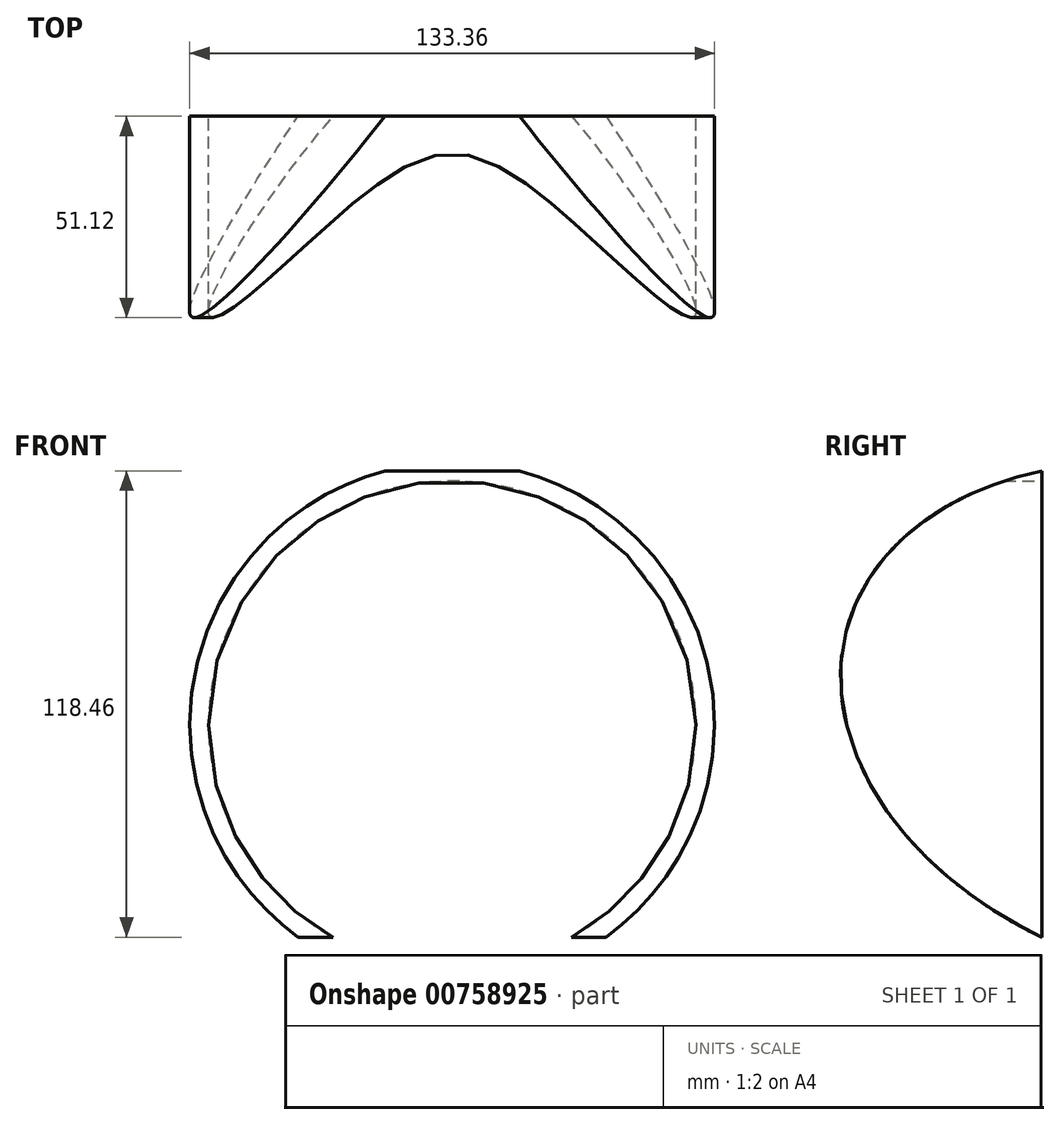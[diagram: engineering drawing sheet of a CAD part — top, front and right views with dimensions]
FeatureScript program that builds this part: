
annotation { "Feature Type Name" : "Feature", "Feature Type Description" : "" }
export const myFeature = defineFeature(function(context is Context, id is Id, definition is map)
    precondition{}
    {
        {
            var Q0;
            Q0=qCreatedBy(makeId("Front.planeOp"),FACE);
            var sketch = newSketch(context, id + "F0", { "sketchPlane" : qUnion([Q0])});
            skArc(sketch, "E0", {"start": v(63.5, 0) * mm, "mid": v(0, 63.5) * mm, "end": v(-63.5, 0) * mm});
            skArc(sketch, "E1", {"start": v(61.9, 1.59) * mm, "mid": v(43.78, 43.78) * mm, "end": v(1.59, 61.9) * mm});
            skArc(sketch, "E2", {"start": v(15.19, 36.67) * mm, "mid": v(8.52, 38.76) * mm, "end": v(1.59, 39.66) * mm});
            skLineSegment(sketch, "E3.0", {"start": v(1.59, 39.66) * mm, "end": v(1.59, 61.9) * mm});
            skLineSegment(sketch, "E4.0", {"start": v(-1.59, 39.66) * mm, "end": v(-1.59, 61.9) * mm});
            skLineSegment(sketch, "E5.1.0", {"start": v(0, -0.01) * mm, "end": v(0, 0) * mm});
            skLineSegment(sketch, "E5.6.1", {"start": v(-1.59, -3.83) * mm, "end": v(-25.8, -28.04) * mm});
            skLineSegment(sketch, "E5.7.1", {"start": v(-13.7, -37.24) * mm, "end": v(-22.22, -57.79) * mm});
            skLineSegment(sketch, "E5.7.2", {"start": v(-16.64, -36.03) * mm, "end": v(-25.15, -56.57) * mm});
            skLineSegment(sketch, "E5.8.1", {"start": v(1.59, -3.83) * mm, "end": v(1.59, -38.07) * mm});
            skLineSegment(sketch, "E5.8.2", {"start": v(-1.59, -3.83) * mm, "end": v(-1.59, -38.07) * mm});
            skLineSegment(sketch, "E5.9.1", {"start": v(16.64, -36.03) * mm, "end": v(25.15, -56.57) * mm});
            skLineSegment(sketch, "E5.9.2", {"start": v(13.7, -37.24) * mm, "end": v(22.22, -57.79) * mm});
            skLineSegment(sketch, "E6", {"start": v(63.5, 0) * mm, "end": v(63.5, 63.64) * mm});
            skLineSegment(sketch, "E7", {"start": v(23.7, 63.5) * mm, "end": v(63.5, 63.5) * mm});
            skLineSegment(sketch, "E8", {"start": v(-63.5, 0) * mm, "end": v(-61.9, 63.5) * mm});
            skLineSegment(sketch, "E9", {"start": v(-61.9, 63.5) * mm, "end": v(-23.7, 63.5) * mm});
            skLineSegment(sketch, "E10", {"start": v(-23.7, 58.91) * mm, "end": v(-23.7, 63.5) * mm});
            skLineSegment(sketch, "E11", {"start": v(23.7, 58.91) * mm, "end": v(23.7, 63.5) * mm});
            skPoint(sketch, "E5.12.0.end.orphan", {"position": v(61.91, 0) * mm});
            skPoint(sketch, "E12.orphan", {"position": v(0, 63.5) * mm});
            skPoint(sketch, "E5.4.2.end.orphan", {"position": v(-61.9, 1.59) * mm});
            skPoint(sketch, "E5.4.0.end.orphan", {"position": v(-61.91, 0) * mm});
            skArc(sketch, "E13.trimOffspring", {"start": v(-63.5, 0) * mm, "mid": v(0, -63.5) * mm, "end": v(63.5, 0) * mm});
            skLineSegment(sketch, "E14", {"start": v(0, 0) * mm, "end": v(0, -0.01) * mm});
            skArc(sketch, "E15.trimOffspring", {"start": v(-61.9, 1.59) * mm, "mid": v(-61.01, -10.52) * mm, "end": v(-57.79, -22.22) * mm});
            skArc(sketch, "E16.trimOffspring", {"start": v(-57.79, -22.22) * mm, "mid": v(-52.34, -33.07) * mm, "end": v(-44.89, -42.64) * mm});
            skPoint(sketch, "E17.trimOffspring.end.orphan", {"position": v(-44.92, -44.89) * mm});
            skPoint(sketch, "E18.trimOffspring.end.orphan", {"position": v(44.89, -44.92) * mm});
            skArc(sketch, "E19.trimOffspring", {"start": v(44.89, -42.64) * mm, "mid": v(57.79, -22.22) * mm, "end": v(61.9, 1.59) * mm});
            skArc(sketch, "E20.trimOffspring", {"start": v(29.16, -26.92) * mm, "mid": v(38.92, 7.74) * mm, "end": v(16.64, 36.03) * mm});
            skArc(sketch, "E21.trimOffspring", {"start": v(-13.7, -37.24) * mm, "mid": v(-7.74, -38.92) * mm, "end": v(-1.59, -39.66) * mm});
            skArc(sketch, "E22.trimOffspring", {"start": v(1.59, -39.66) * mm, "mid": v(7.74, -38.92) * mm, "end": v(13.7, -37.24) * mm});
            skArc(sketch, "E23.trimOffspring", {"start": v(16.64, -36.03) * mm, "mid": v(22.05, -33) * mm, "end": v(26.92, -29.16) * mm});
            skLineSegment(sketch, "E24.trimOffspring", {"start": v(26.92, -29.16) * mm, "end": v(42.64, -44.89) * mm});
            skLineSegment(sketch, "E25.trimOffspring", {"start": v(-26.92, -29.16) * mm, "end": v(-42.64, -44.89) * mm});
            skLineSegment(sketch, "E26.trimOffspring", {"start": v(15.19, 36.67) * mm, "end": v(23.7, 57.2) * mm});
            skLineSegment(sketch, "E27.trimOffspring", {"start": v(-15.19, 36.67) * mm, "end": v(-23.7, 57.2) * mm});
            skPoint(sketch, "E28.orphan", {"position": v(37.24, -13.7) * mm});
            skLineSegment(sketch, "E29", {"start": v(-61.9, 1.59) * mm, "end": v(-60.3, 63.5) * mm});
            skLineSegment(sketch, "E30", {"start": v(61.9, 1.59) * mm, "end": v(61.9, 63.5) * mm});
            skLineSegment(sketch, "E31.trimOffspring", {"start": v(-1.59, -39.66) * mm, "end": v(-1.59, -61.9) * mm});
            skArc(sketch, "E32.trimOffspring", {"start": v(1.59, -38.07) * mm, "mid": v(14.58, -35.2) * mm, "end": v(25.8, -28.04) * mm});
            skLineSegment(sketch, "E33.trimOffspring", {"start": v(1.59, -39.66) * mm, "end": v(1.59, -61.9) * mm});
            skArc(sketch, "E34.trimOffspring", {"start": v(-25.8, -28.04) * mm, "mid": v(-14.58, -35.2) * mm, "end": v(-1.59, -38.07) * mm});
            skLineSegment(sketch, "E35.trimOffspring", {"start": v(-29.16, -26.92) * mm, "end": v(-44.89, -42.64) * mm});
            skLineSegment(sketch, "E36.trimOffspring", {"start": v(29.16, -26.92) * mm, "end": v(44.89, -42.64) * mm});
            skLineSegment(sketch, "E37.trimOffspring", {"start": v(1.59, -3.83) * mm, "end": v(25.8, -28.04) * mm});
            skArc(sketch, "E38.trimOffspring", {"start": v(-26.92, -29.16) * mm, "mid": v(-22.05, -33) * mm, "end": v(-16.64, -36.03) * mm});
            skArc(sketch, "E39.trimOffspring", {"start": v(-42.64, -44.89) * mm, "mid": v(-34.4, -51.48) * mm, "end": v(-25.15, -56.57) * mm});
            skArc(sketch, "E40.trimOffspring", {"start": v(-22.22, -57.79) * mm, "mid": v(-12.08, -60.72) * mm, "end": v(-1.59, -61.9) * mm});
            skArc(sketch, "E41.trimOffspring", {"start": v(1.59, -61.9) * mm, "mid": v(12.08, -60.72) * mm, "end": v(22.22, -57.79) * mm});
            skArc(sketch, "E42.trimOffspring", {"start": v(25.15, -56.57) * mm, "mid": v(34.4, -51.48) * mm, "end": v(42.64, -44.89) * mm});
            skPoint(sketch, "E43.end.orphan", {"position": v(0, 61.91) * mm});
            skPoint(sketch, "E43.start.orphan", {"position": v(0, 39.69) * mm});
            skArc(sketch, "E44.trimOffspring", {"start": v(-1.59, 61.9) * mm, "mid": v(-43.78, 43.78) * mm, "end": v(-61.9, 1.59) * mm});
            skArc(sketch, "E45.trimOffspring", {"start": v(-1.59, 39.66) * mm, "mid": v(-8.52, 38.76) * mm, "end": v(-15.19, 36.67) * mm});
            skLineSegment(sketch, "E46.0", {"start": v(16.64, 36.03) * mm, "end": v(25.28, 56.88) * mm});
            skLineSegment(sketch, "E47.0", {"start": v(-16.64, 36.03) * mm, "end": v(-25.28, 56.88) * mm});
            skLineSegment(sketch, "E48.0", {"start": v(-25.28, 56.88) * mm, "end": v(-25.28, 63.5) * mm});
            skLineSegment(sketch, "E49.0", {"start": v(25.28, 56.88) * mm, "end": v(25.28, 63.5) * mm});
            skArc(sketch, "E50.trimOffspring", {"start": v(-16.64, 36.03) * mm, "mid": v(-38.92, 7.74) * mm, "end": v(-29.16, -26.92) * mm});
            skArc(sketch, "E51.1.0", {"start": v(28.04, -25.8) * mm, "mid": v(35.2, -14.58) * mm, "end": v(38.07, -1.59) * mm});
            skLineSegment(sketch, "E51.1.1", {"start": v(3.83, -1.59) * mm, "end": v(28.04, -25.8) * mm});
            skLineSegment(sketch, "E51.1.2", {"start": v(3.83, -1.59) * mm, "end": v(38.07, -1.59) * mm});
            skArc(sketch, "E51.2.0", {"start": v(38.07, 1.59) * mm, "mid": v(35.2, 14.58) * mm, "end": v(28.04, 25.8) * mm});
            skLineSegment(sketch, "E51.2.1", {"start": v(3.83, 1.59) * mm, "end": v(38.07, 1.59) * mm});
            skLineSegment(sketch, "E51.2.2", {"start": v(3.83, 1.59) * mm, "end": v(28.04, 25.8) * mm});
            skArc(sketch, "E51.3.0", {"start": v(25.8, 28.04) * mm, "mid": v(14.58, 35.2) * mm, "end": v(1.59, 38.07) * mm});
            skLineSegment(sketch, "E51.3.1", {"start": v(1.59, 3.83) * mm, "end": v(25.8, 28.04) * mm});
            skLineSegment(sketch, "E51.3.2", {"start": v(1.59, 3.83) * mm, "end": v(1.59, 38.07) * mm});
            skLineSegment(sketch, "E51.4.1", {"start": v(-1.59, 3.83) * mm, "end": v(-1.59, 38.07) * mm});
            skLineSegment(sketch, "E51.4.2", {"start": v(-1.59, 3.83) * mm, "end": v(-25.8, 28.04) * mm});
            skArc(sketch, "E51.5.0", {"start": v(-28.04, 25.8) * mm, "mid": v(-35.2, 14.58) * mm, "end": v(-38.07, 1.59) * mm});
            skLineSegment(sketch, "E51.5.1", {"start": v(-3.83, 1.59) * mm, "end": v(-28.04, 25.8) * mm});
            skLineSegment(sketch, "E51.5.2", {"start": v(-3.83, 1.59) * mm, "end": v(-38.07, 1.59) * mm});
            skArc(sketch, "E51.6.0", {"start": v(-38.07, -1.59) * mm, "mid": v(-35.2, -14.58) * mm, "end": v(-28.04, -25.8) * mm});
            skLineSegment(sketch, "E51.6.1", {"start": v(-3.83, -1.59) * mm, "end": v(-38.07, -1.59) * mm});
            skLineSegment(sketch, "E51.6.2", {"start": v(-3.83, -1.59) * mm, "end": v(-28.04, -25.8) * mm});
            skCircle(sketch, "E52.converted", {"center": v(0, 0) * mm, "radius": 38.1 * mm});
            skCircle(sketch, "E53", {"center": v(0, 0) * mm, "radius": 66.68 * mm});
            skCircle(sketch, "E54.converted", {"center": v(0, 0) * mm, "radius": 65.09 * mm});
            skSolve(sketch);
        }
        {
            var Q0;
            Q0=qCreatedBy(makeId("Front.planeOp"),FACE);
            var sketch = newSketch(context, id + "F1", { "sketchPlane" : qUnion([Q0])});
            skCircle(sketch, "E55", {"center": v(0, 0) * mm, "radius": 63.5 * mm});
            skCircle(sketch, "E56", {"center": v(0, 0) * mm, "radius": 38.1 * mm});
            skCircle(sketch, "E57", {"center": v(0, 0) * mm, "radius": 61.91 * mm});
            skLineSegment(sketch, "E58.4.0", {"start": v(-39.69, 0) * mm, "end": v(-65.09, 0) * mm});
            skLineSegment(sketch, "E58.4.1", {"start": v(-39.66, -1.59) * mm, "end": v(-61.9, -1.59) * mm});
            skLineSegment(sketch, "E58.4.2", {"start": v(-39.66, 1.59) * mm, "end": v(-61.9, 1.59) * mm});
            skLineSegment(sketch, "E58.5.0", {"start": v(-36.67, -15.19) * mm, "end": v(-57.2, -23.7) * mm});
            skLineSegment(sketch, "E58.5.1", {"start": v(-36.03, -16.64) * mm, "end": v(-56.57, -25.15) * mm});
            skLineSegment(sketch, "E58.5.2", {"start": v(-37.24, -13.7) * mm, "end": v(-57.79, -22.22) * mm});
            skLineSegment(sketch, "E58.6.0", {"start": v(-28.06, -28.06) * mm, "end": v(-43.78, -43.78) * mm});
            skLineSegment(sketch, "E58.6.1", {"start": v(-26.92, -29.16) * mm, "end": v(-42.64, -44.89) * mm});
            skLineSegment(sketch, "E58.6.2", {"start": v(-29.16, -26.92) * mm, "end": v(-44.89, -42.64) * mm});
            skLineSegment(sketch, "E58.7.0", {"start": v(-15.19, -36.67) * mm, "end": v(-23.7, -57.2) * mm});
            skLineSegment(sketch, "E58.7.1", {"start": v(-13.7, -37.24) * mm, "end": v(-22.22, -57.79) * mm});
            skLineSegment(sketch, "E58.7.2", {"start": v(-16.64, -36.03) * mm, "end": v(-25.15, -56.57) * mm});
            skLineSegment(sketch, "E58.8.0", {"start": v(0, -39.69) * mm, "end": v(0, -61.91) * mm});
            skLineSegment(sketch, "E58.8.1", {"start": v(1.59, -39.66) * mm, "end": v(1.59, -61.9) * mm});
            skLineSegment(sketch, "E58.8.2", {"start": v(-1.59, -39.66) * mm, "end": v(-1.59, -61.9) * mm});
            skLineSegment(sketch, "E58.9.0", {"start": v(15.19, -36.67) * mm, "end": v(23.7, -57.2) * mm});
            skLineSegment(sketch, "E58.9.1", {"start": v(16.64, -36.03) * mm, "end": v(25.15, -56.57) * mm});
            skLineSegment(sketch, "E58.9.2", {"start": v(13.7, -37.24) * mm, "end": v(22.22, -57.79) * mm});
            skLineSegment(sketch, "E58.10.0", {"start": v(28.06, -28.06) * mm, "end": v(43.78, -43.78) * mm});
            skLineSegment(sketch, "E58.10.1", {"start": v(29.16, -26.92) * mm, "end": v(44.89, -42.64) * mm});
            skLineSegment(sketch, "E58.10.2", {"start": v(26.92, -29.16) * mm, "end": v(42.64, -44.89) * mm});
            skLineSegment(sketch, "E58.11.0", {"start": v(36.67, -15.19) * mm, "end": v(57.2, -23.7) * mm});
            skLineSegment(sketch, "E58.11.1", {"start": v(37.24, -13.7) * mm, "end": v(57.79, -22.22) * mm});
            skLineSegment(sketch, "E58.11.2", {"start": v(36.03, -16.64) * mm, "end": v(56.57, -25.15) * mm});
            skLineSegment(sketch, "E58.12.0", {"start": v(39.69, 0) * mm, "end": v(65.09, 0) * mm});
            skLineSegment(sketch, "E58.12.1", {"start": v(39.66, 1.59) * mm, "end": v(61.9, 1.59) * mm});
            skLineSegment(sketch, "E58.12.2", {"start": v(39.66, -1.59) * mm, "end": v(61.9, -1.59) * mm});
            skCircle(sketch, "E59.converted", {"center": v(0, 0) * mm, "radius": 39.69 * mm});
            skCircle(sketch, "E60", {"center": v(0, 0) * mm, "radius": 65.09 * mm});
            skPoint(sketch, "E61.orphan", {"position": v(61.91, 0) * mm});
            skPoint(sketch, "E62.orphan", {"position": v(-61.91, 0) * mm});
            skCircle(sketch, "E63", {"center": v(0, 0) * mm, "radius": 50.8 * mm});
            skCircle(sketch, "E64", {"center": v(0, 0) * mm, "radius": 49.21 * mm});
            skCircle(sketch, "E65", {"center": v(0, 0) * mm, "radius": 36.51 * mm});
            skCircle(sketch, "E66", {"center": v(0, 0) * mm, "radius": 66.68 * mm});
            skCircle(sketch, "E67", {"center": v(0, 0) * mm, "radius": 57.15 * mm});
            skSolve(sketch);
        }
        {
            var Q0;
            Q0=qCreatedBy(makeId("Front.planeOp"),FACE);
            var sketch = newSketch(context, id + "F2", { "sketchPlane" : qUnion([Q0])});
            skCircle(sketch, "E68", {"center": v(0, 0) * mm, "radius": 63.5 * mm});
            skCircle(sketch, "E69", {"center": v(0, 0) * mm, "radius": 38.1 * mm});
            skArc(sketch, "E70", {"start": v(56.57, 25.15) * mm, "mid": v(51.48, 34.4) * mm, "end": v(44.89, 42.64) * mm});
            skArc(sketch, "E71", {"start": v(36.03, 16.64) * mm, "mid": v(33, 22.05) * mm, "end": v(29.16, 26.92) * mm});
            skLineSegment(sketch, "E72.0", {"start": v(1.59, 39.66) * mm, "end": v(1.59, 61.9) * mm});
            skLineSegment(sketch, "E73.0", {"start": v(-1.59, 39.66) * mm, "end": v(-1.59, 61.9) * mm});
            skLineSegment(sketch, "E74.1.1", {"start": v(-16.64, 36.03) * mm, "end": v(-25.15, 56.57) * mm});
            skLineSegment(sketch, "E74.1.2", {"start": v(-13.7, 37.24) * mm, "end": v(-22.22, 57.79) * mm});
            skLineSegment(sketch, "E74.2.1", {"start": v(-29.16, 26.92) * mm, "end": v(-44.89, 42.64) * mm});
            skLineSegment(sketch, "E74.2.2", {"start": v(-26.92, 29.16) * mm, "end": v(-42.64, 44.89) * mm});
            skLineSegment(sketch, "E74.3.1", {"start": v(-37.24, 13.7) * mm, "end": v(-57.79, 22.22) * mm});
            skLineSegment(sketch, "E74.3.2", {"start": v(-36.03, 16.64) * mm, "end": v(-56.57, 25.15) * mm});
            skLineSegment(sketch, "E74.4.1", {"start": v(-39.66, -1.59) * mm, "end": v(-61.9, -1.59) * mm});
            skLineSegment(sketch, "E74.4.2", {"start": v(-39.66, 1.59) * mm, "end": v(-61.9, 1.59) * mm});
            skLineSegment(sketch, "E74.5.1", {"start": v(-36.03, -16.64) * mm, "end": v(-56.57, -25.15) * mm});
            skLineSegment(sketch, "E74.5.2", {"start": v(-37.24, -13.7) * mm, "end": v(-57.79, -22.22) * mm});
            skLineSegment(sketch, "E74.6.1", {"start": v(-26.92, -29.16) * mm, "end": v(-42.64, -44.89) * mm});
            skLineSegment(sketch, "E74.6.2", {"start": v(-29.16, -26.92) * mm, "end": v(-44.89, -42.64) * mm});
            skLineSegment(sketch, "E74.7.1", {"start": v(-13.7, -37.24) * mm, "end": v(-22.22, -57.79) * mm});
            skLineSegment(sketch, "E74.7.2", {"start": v(-16.64, -36.03) * mm, "end": v(-25.15, -56.57) * mm});
            skLineSegment(sketch, "E74.8.1", {"start": v(1.59, -39.66) * mm, "end": v(1.59, -61.9) * mm});
            skLineSegment(sketch, "E74.8.2", {"start": v(-1.59, -39.66) * mm, "end": v(-1.59, -61.9) * mm});
            skLineSegment(sketch, "E74.9.1", {"start": v(16.64, -36.03) * mm, "end": v(25.15, -56.57) * mm});
            skLineSegment(sketch, "E74.9.2", {"start": v(13.7, -37.24) * mm, "end": v(22.22, -57.79) * mm});
            skLineSegment(sketch, "E74.10.1", {"start": v(29.16, -26.92) * mm, "end": v(44.89, -42.64) * mm});
            skLineSegment(sketch, "E74.10.2", {"start": v(26.92, -29.16) * mm, "end": v(42.64, -44.89) * mm});
            skLineSegment(sketch, "E74.11.1", {"start": v(37.24, -13.7) * mm, "end": v(57.79, -22.22) * mm});
            skLineSegment(sketch, "E74.11.2", {"start": v(36.03, -16.64) * mm, "end": v(56.57, -25.15) * mm});
            skLineSegment(sketch, "E74.12.1", {"start": v(39.66, 1.59) * mm, "end": v(61.9, 1.59) * mm});
            skLineSegment(sketch, "E74.12.2", {"start": v(39.66, -1.59) * mm, "end": v(61.9, -1.59) * mm});
            skLineSegment(sketch, "E74.13.1", {"start": v(36.03, 16.64) * mm, "end": v(56.57, 25.15) * mm});
            skLineSegment(sketch, "E74.13.2", {"start": v(37.24, 13.7) * mm, "end": v(57.79, 22.22) * mm});
            skLineSegment(sketch, "E74.14.1", {"start": v(26.92, 29.16) * mm, "end": v(42.64, 44.89) * mm});
            skLineSegment(sketch, "E74.14.2", {"start": v(29.16, 26.92) * mm, "end": v(44.89, 42.64) * mm});
            skLineSegment(sketch, "E74.15.1", {"start": v(13.7, 37.24) * mm, "end": v(22.22, 57.79) * mm});
            skLineSegment(sketch, "E74.15.2", {"start": v(16.64, 36.03) * mm, "end": v(25.15, 56.57) * mm});
            skArc(sketch, "E75.trimOffspring", {"start": v(39.66, 1.59) * mm, "mid": v(38.92, 7.74) * mm, "end": v(37.24, 13.7) * mm});
            skArc(sketch, "E76.trimOffspring", {"start": v(57.79, -22.22) * mm, "mid": v(60.72, -12.08) * mm, "end": v(61.9, -1.59) * mm});
            skArc(sketch, "E77.trimOffspring", {"start": v(37.24, -13.7) * mm, "mid": v(38.92, -7.74) * mm, "end": v(39.66, -1.59) * mm});
            skArc(sketch, "E78.trimOffspring", {"start": v(61.9, 1.59) * mm, "mid": v(60.72, 12.08) * mm, "end": v(57.79, 22.22) * mm});
            skArc(sketch, "E79.trimOffspring", {"start": v(-26.92, -29.16) * mm, "mid": v(-22.05, -33) * mm, "end": v(-16.64, -36.03) * mm});
            skArc(sketch, "E80.trimOffspring", {"start": v(-42.64, -44.89) * mm, "mid": v(-34.4, -51.48) * mm, "end": v(-25.15, -56.57) * mm});
            skArc(sketch, "E81.trimOffspring", {"start": v(-22.22, -57.79) * mm, "mid": v(-12.08, -60.72) * mm, "end": v(-1.59, -61.9) * mm});
            skArc(sketch, "E82.trimOffspring", {"start": v(-13.7, -37.24) * mm, "mid": v(-7.74, -38.92) * mm, "end": v(-1.59, -39.66) * mm});
            skArc(sketch, "E83.trimOffspring", {"start": v(1.59, -39.66) * mm, "mid": v(7.74, -38.92) * mm, "end": v(13.7, -37.24) * mm});
            skArc(sketch, "E84.trimOffspring", {"start": v(1.59, -61.9) * mm, "mid": v(12.08, -60.72) * mm, "end": v(22.22, -57.79) * mm});
            skArc(sketch, "E85.trimOffspring", {"start": v(16.64, -36.03) * mm, "mid": v(22.05, -33) * mm, "end": v(26.92, -29.16) * mm});
            skArc(sketch, "E86.trimOffspring", {"start": v(25.15, -56.57) * mm, "mid": v(34.4, -51.48) * mm, "end": v(42.64, -44.89) * mm});
            skArc(sketch, "E87.trimOffspring", {"start": v(29.16, -26.92) * mm, "mid": v(33, -22.05) * mm, "end": v(36.03, -16.64) * mm});
            skArc(sketch, "E88.trimOffspring", {"start": v(44.89, -42.64) * mm, "mid": v(51.48, -34.4) * mm, "end": v(56.57, -25.15) * mm});
            skArc(sketch, "E89.trimOffspring", {"start": v(-25.15, 56.57) * mm, "mid": v(-34.4, 51.48) * mm, "end": v(-42.64, 44.89) * mm});
            skArc(sketch, "E90.trimOffspring", {"start": v(-16.64, 36.03) * mm, "mid": v(-22.05, 33) * mm, "end": v(-26.92, 29.16) * mm});
            skArc(sketch, "E91.trimOffspring", {"start": v(13.7, 37.24) * mm, "mid": v(7.74, 38.92) * mm, "end": v(1.59, 39.66) * mm});
            skArc(sketch, "E92.trimOffspring", {"start": v(42.64, 44.89) * mm, "mid": v(34.4, 51.48) * mm, "end": v(25.15, 56.57) * mm});
            skArc(sketch, "E93.trimOffspring", {"start": v(26.92, 29.16) * mm, "mid": v(22.05, 33) * mm, "end": v(16.64, 36.03) * mm});
            skArc(sketch, "E94.trimOffspring", {"start": v(-1.59, 61.9) * mm, "mid": v(-12.08, 60.72) * mm, "end": v(-22.22, 57.79) * mm});
            skArc(sketch, "E95.trimOffspring", {"start": v(-1.59, 39.66) * mm, "mid": v(-7.74, 38.92) * mm, "end": v(-13.7, 37.24) * mm});
            skArc(sketch, "E96.trimOffspring", {"start": v(22.22, 57.79) * mm, "mid": v(12.08, 60.72) * mm, "end": v(1.59, 61.9) * mm});
            skArc(sketch, "E97.trimOffspring", {"start": v(-29.16, 26.92) * mm, "mid": v(-33, 22.05) * mm, "end": v(-36.03, 16.64) * mm});
            skArc(sketch, "E98.trimOffspring", {"start": v(-44.89, 42.64) * mm, "mid": v(-51.48, 34.4) * mm, "end": v(-56.57, 25.15) * mm});
            skArc(sketch, "E99.trimOffspring", {"start": v(-37.24, 13.7) * mm, "mid": v(-38.92, 7.74) * mm, "end": v(-39.66, 1.59) * mm});
            skArc(sketch, "E100.trimOffspring", {"start": v(-57.79, 22.22) * mm, "mid": v(-60.72, 12.08) * mm, "end": v(-61.9, 1.59) * mm});
            skArc(sketch, "E101.trimOffspring", {"start": v(-61.9, -1.59) * mm, "mid": v(-60.72, -12.08) * mm, "end": v(-57.79, -22.22) * mm});
            skArc(sketch, "E102.trimOffspring", {"start": v(-39.66, -1.59) * mm, "mid": v(-38.92, -7.74) * mm, "end": v(-37.24, -13.7) * mm});
            skArc(sketch, "E103.trimOffspring", {"start": v(-36.03, -16.64) * mm, "mid": v(-33, -22.05) * mm, "end": v(-29.16, -26.92) * mm});
            skArc(sketch, "E104.trimOffspring", {"start": v(-56.57, -25.15) * mm, "mid": v(-51.48, -34.4) * mm, "end": v(-44.89, -42.64) * mm});
            skCircle(sketch, "E105", {"center": v(0, 0) * mm, "radius": 0.8 * mm});
            skSolve(sketch);
        }
        {
            var Q0;
            {var subQ5=sQuery(id+"F0.wireOp",EDGE,"E30");var subQ7=sQuery(id+"F0.wireOp",EDGE,"E0");var subQ9=makeQuery(id+"F0.imprint","INTERSECT",VERTEX,{"derivedFrom":[subQ7,subQ5]});Q0=makeQuery(id+"F0.imprint","IMPRINT",FACE,{"disambiguationData":[TD([[makeQuery(id+"F0.imprint","IMPRINT",EDGE,{"disambiguationData":[TD([[subQ9,-1.0]])],"derivedFrom":subQ7}),1.0]])]});}
            var Q1;
            {var subQ0=sQuery(id+"F0.wireOp",EDGE,"E51.1.1");Q1=makeQuery(id+"F0.imprint","IMPRINT",FACE,{"disambiguationData":[TD([[makeQuery(id+"F0.imprint","IMPRINT",EDGE,{"derivedFrom":subQ0}),1.0]])]});}
            var Q2;
            {var subQ0=sQuery(id+"F0.wireOp",EDGE,"E48.0");var subQ7=sQuery(id+"F0.wireOp",EDGE,"E0");var subQ9=makeQuery(id+"F0.imprint","INTERSECT",VERTEX,{"derivedFrom":[subQ7,subQ0]});Q2=makeQuery(id+"F0.imprint","IMPRINT",FACE,{"disambiguationData":[TD([[makeQuery(id+"F0.imprint","IMPRINT",EDGE,{"disambiguationData":[TD([[subQ9,-1.0]])],"derivedFrom":subQ7}),1.0]])]});}
            var Q3;
            {var subQ0=sQuery(id+"F0.wireOp",EDGE,"E51.2.1");Q3=makeQuery(id+"F0.imprint","IMPRINT",FACE,{"disambiguationData":[TD([[makeQuery(id+"F0.imprint","IMPRINT",EDGE,{"derivedFrom":subQ0}),1.0]])]});}
            var Q4;
            {var subQ1=sQuery(id+"F0.wireOp",EDGE,"E19.trimOffspring");Q4=makeQuery(id+"F0.imprint","IMPRINT",FACE,{"disambiguationData":[TD([[makeQuery(id+"F0.imprint","IMPRINT",EDGE,{"derivedFrom":subQ1}),1.0]])]});}
            var Q5;
            {var subQ0=sQuery(id+"F0.wireOp",EDGE,"E51.5.1");Q5=makeQuery(id+"F0.imprint","IMPRINT",FACE,{"disambiguationData":[TD([[makeQuery(id+"F0.imprint","IMPRINT",EDGE,{"derivedFrom":subQ0}),1.0]])]});}
            var Q6;
            {var subQ1=sQuery(id+"F0.wireOp",EDGE,"E15.trimOffspring");Q6=makeQuery(id+"F0.imprint","IMPRINT",FACE,{"disambiguationData":[TD([[makeQuery(id+"F0.imprint","IMPRINT",EDGE,{"derivedFrom":subQ1}),1.0]])]});}
            var Q7;
            {var subQ23=sQuery(id+"F0.wireOp",EDGE,"E3.0");Q7=makeQuery(id+"F0.imprint","IMPRINT",FACE,{"disambiguationData":[TD([[makeQuery(id+"F0.imprint","IMPRINT",EDGE,{"derivedFrom":subQ23}),1.0]])]});}
            var Q8;
            {var subQ0=sQuery(id+"F0.wireOp",EDGE,"E51.6.1");Q8=makeQuery(id+"F0.imprint","IMPRINT",FACE,{"disambiguationData":[TD([[makeQuery(id+"F0.imprint","IMPRINT",EDGE,{"derivedFrom":subQ0}),1.0]])]});}
            var Q9;
            {var subQ5=sQuery(id+"F0.wireOp",EDGE,"E5.8.1");Q9=makeQuery(id+"F0.imprint","IMPRINT",FACE,{"disambiguationData":[TD([[makeQuery(id+"F0.imprint","IMPRINT",EDGE,{"derivedFrom":subQ5}),-1.0]])]});}
            extrude(context, id + "F3", {"entities" : qUnion([Q0, Q1, Q2, Q3, Q4, Q5, Q6, Q7, Q8, Q9]), "oppositeDirection" : true, "depth" : 889 * mm, "offsetDistance" : 25.4 * mm, "hasSecondDirection" : true, "secondDirectionOppositeDirection" : true, "secondDirectionDepth" : 38.1 * mm});
        }
        {
            var Q0;
            Q0=makeQuery(id+"F0.imprint","IMPRINT",FACE,{"disambiguationData":[TD([[makeQuery(id+"F0.imprint","IMPRINT",EDGE,{"derivedFrom":sQuery(id+"F0.wireOp",EDGE,"E0")}),1.0]])]});
            var Q1;
            {var subQ5=sQuery(id+"F0.wireOp",EDGE,"E5.8.1");Q1=makeQuery(id+"F0.imprint","IMPRINT",FACE,{"disambiguationData":[TD([[makeQuery(id+"F0.imprint","IMPRINT",EDGE,{"derivedFrom":subQ5}),-1.0]])]});}
            var Q2;
            {var subQ0=sQuery(id+"F0.wireOp",EDGE,"E51.2.1");Q2=makeQuery(id+"F0.imprint","IMPRINT",FACE,{"disambiguationData":[TD([[makeQuery(id+"F0.imprint","IMPRINT",EDGE,{"derivedFrom":subQ0}),1.0]])]});}
            var Q3;
            {var subQ0=sQuery(id+"F0.wireOp",EDGE,"E51.1.1");Q3=makeQuery(id+"F0.imprint","IMPRINT",FACE,{"disambiguationData":[TD([[makeQuery(id+"F0.imprint","IMPRINT",EDGE,{"derivedFrom":subQ0}),1.0]])]});}
            var Q4;
            {var subQ0=sQuery(id+"F0.wireOp",EDGE,"E51.5.1");Q4=makeQuery(id+"F0.imprint","IMPRINT",FACE,{"disambiguationData":[TD([[makeQuery(id+"F0.imprint","IMPRINT",EDGE,{"derivedFrom":subQ0}),1.0]])]});}
            var Q5;
            {var subQ0=sQuery(id+"F0.wireOp",EDGE,"E51.6.1");Q5=makeQuery(id+"F0.imprint","IMPRINT",FACE,{"disambiguationData":[TD([[makeQuery(id+"F0.imprint","IMPRINT",EDGE,{"derivedFrom":subQ0}),1.0]])]});}
            var Q6;
            {var subQ0=sQuery(id+"F0.wireOp",EDGE,"E8");var subQ1=sQuery(id+"F0.wireOp",EDGE,"E0");var subQ2=makeQuery(id+"F0.imprint","INTERSECT",VERTEX,{"derivedFrom":[subQ1,subQ0]});Q6=makeQuery(id+"F0.imprint","IMPRINT",FACE,{"disambiguationData":[TD([[makeQuery(id+"F0.imprint","IMPRINT",EDGE,{"disambiguationData":[TD([[subQ2,1.0]])],"derivedFrom":subQ1}),-1.0]])]});}
            var Q7;
            {var subQ0=sQuery(id+"F0.wireOp",EDGE,"E6");var subQ5=sQuery(id+"F0.wireOp",EDGE,"E7");var subQ6=makeQuery(id+"F0.imprint","INTERSECT",VERTEX,{"derivedFrom":[subQ0,subQ5]});Q7=makeQuery(id+"F0.imprint","IMPRINT",FACE,{"disambiguationData":[TD([[makeQuery(id+"F0.imprint","IMPRINT",EDGE,{"disambiguationData":[TD([[subQ6,1.0]])],"derivedFrom":subQ5}),-1.0]])]});}
            var Q8;
            {var subQ0=sQuery(id+"F0.wireOp",EDGE,"E10");Q8=makeQuery(id+"F0.imprint","IMPRINT",FACE,{"disambiguationData":[TD([[makeQuery(id+"F0.imprint","IMPRINT",EDGE,{"derivedFrom":subQ0}),1.0]])]});}
            var Q9;
            {var subQ0=sQuery(id+"F0.wireOp",EDGE,"E11");Q9=makeQuery(id+"F0.imprint","IMPRINT",FACE,{"disambiguationData":[TD([[makeQuery(id+"F0.imprint","IMPRINT",EDGE,{"derivedFrom":subQ0}),-1.0]])]});}
            var Q10;
            {var subQ0=sQuery(id+"F0.wireOp",EDGE,"E13.trimOffspring");Q10=makeQuery(id+"F0.imprint","IMPRINT",FACE,{"disambiguationData":[TD([[makeQuery(id+"F0.imprint","IMPRINT",EDGE,{"derivedFrom":subQ0}),-1.0]])]});}
            var Q11;
            {var subQ5=sQuery(id+"F0.wireOp",EDGE,"E6");var subQ7=makeQuery(id+"F0.imprint","INTERSECT",VERTEX,{"derivedFrom":[subQ5,sQuery(id+"F0.wireOp",EDGE,"bf8f1726-02c7-49f6-86c3-abb20af7b560.trimOffspring")]});Q11=makeQuery(id+"F0.imprint","IMPRINT",FACE,{"disambiguationData":[TD([[makeQuery(id+"F0.imprint","IMPRINT",EDGE,{"disambiguationData":[TD([[subQ7,-1.0]])],"derivedFrom":subQ5}),1.0]])]});}
            var Q12;
            {var subQ0=sQuery(id+"F0.wireOp",EDGE,"E9");var subQ1=sQuery(id+"F0.wireOp",EDGE,"E8");var subQ2=makeQuery(id+"F0.imprint","INTERSECT",VERTEX,{"derivedFrom":[subQ1,subQ0]});Q12=makeQuery(id+"F0.imprint","IMPRINT",FACE,{"disambiguationData":[TD([[makeQuery(id+"F0.imprint","IMPRINT",EDGE,{"disambiguationData":[TD([[subQ2,1.0]])],"derivedFrom":subQ1}),-1.0]])]});}
            var Q13;
            {var subQ1=sQuery(id+"F0.wireOp",EDGE,"E0");var subQ3=sQuery(id+"F0.wireOp",EDGE,"E30");var subQ4=makeQuery(id+"F0.imprint","INTERSECT",VERTEX,{"derivedFrom":[subQ1,subQ3]});Q13=makeQuery(id+"F0.imprint","IMPRINT",FACE,{"disambiguationData":[TD([[makeQuery(id+"F0.imprint","IMPRINT",EDGE,{"disambiguationData":[TD([[subQ4,-1.0]])],"derivedFrom":subQ3}),-1.0]])]});}
            var Q14;
            {var subQ0=sQuery(id+"F0.wireOp",EDGE,"E53");var subQ1=sQuery(id+"F0.wireOp",EDGE,"E8");var subQ2=makeQuery(id+"F0.imprint","INTERSECT",VERTEX,{"derivedFrom":[subQ1,subQ0]});Q14=makeQuery(id+"F0.imprint","IMPRINT",FACE,{"disambiguationData":[TD([[makeQuery(id+"F0.imprint","IMPRINT",EDGE,{"disambiguationData":[TD([[subQ2,1.0]])],"derivedFrom":subQ1}),-1.0]])]});}
            extrude(context, id + "F4", {"entities" : qUnion([Q0, Q1, Q2, Q3, Q4, Q5, Q6, Q7, Q8, Q9, Q10, Q11, Q12, Q13, Q14]), "endBound" : BoundingType.SYMMETRIC, "depth" : 76.2 * mm, "offsetDistance" : 25.4 * mm});
        }
        {
            var Q0;
            {var subQ0=sQuery(id+"F0.wireOp",EDGE,"E51.1.1");Q0=makeQuery(id+"F0.imprint","IMPRINT",FACE,{"disambiguationData":[TD([[makeQuery(id+"F0.imprint","IMPRINT",EDGE,{"derivedFrom":subQ0}),1.0]])]});}
            var Q1;
            Q1=makeQuery(id+"F0.imprint","IMPRINT",FACE,{"disambiguationData":[TD([[makeQuery(id+"F0.imprint","IMPRINT",EDGE,{"derivedFrom":sQuery(id+"F0.wireOp",EDGE,"E0")}),1.0]])]});
            var Q2;
            {var subQ0=sQuery(id+"F0.wireOp",EDGE,"E51.2.1");Q2=makeQuery(id+"F0.imprint","IMPRINT",FACE,{"disambiguationData":[TD([[makeQuery(id+"F0.imprint","IMPRINT",EDGE,{"derivedFrom":subQ0}),1.0]])]});}
            var Q3;
            Q3=makeQuery(id+"F0.imprint","IMPRINT",FACE,{"disambiguationData":[TD([[makeQuery(id+"F0.imprint","IMPRINT",EDGE,{"derivedFrom":sQuery(id+"F0.wireOp",EDGE,"E19.trimOffspring")}),1.0]])]});
            var Q4;
            {var subQ0=sQuery(id+"F0.wireOp",EDGE,"E51.6.1");Q4=makeQuery(id+"F0.imprint","IMPRINT",FACE,{"disambiguationData":[TD([[makeQuery(id+"F0.imprint","IMPRINT",EDGE,{"derivedFrom":subQ0}),1.0]])]});}
            var Q5;
            {var subQ0=sQuery(id+"F0.wireOp",EDGE,"E51.5.1");Q5=makeQuery(id+"F0.imprint","IMPRINT",FACE,{"disambiguationData":[TD([[makeQuery(id+"F0.imprint","IMPRINT",EDGE,{"derivedFrom":subQ0}),1.0]])]});}
            var Q6;
            {var subQ5=sQuery(id+"F0.wireOp",EDGE,"E5.8.1");Q6=makeQuery(id+"F0.imprint","IMPRINT",FACE,{"disambiguationData":[TD([[makeQuery(id+"F0.imprint","IMPRINT",EDGE,{"derivedFrom":subQ5}),-1.0]])]});}
            var Q7;
            Q7=makeQuery(id+"F0.imprint","IMPRINT",FACE,{"disambiguationData":[TD([[makeQuery(id+"F0.imprint","IMPRINT",EDGE,{"derivedFrom":sQuery(id+"F0.wireOp",EDGE,"E15.trimOffspring")}),1.0]])]});
            var Q8;
            {var subQ0=sQuery(id+"F0.wireOp",EDGE,"E48.0");var subQ7=sQuery(id+"F0.wireOp",EDGE,"E0");var subQ9=makeQuery(id+"F0.imprint","INTERSECT",VERTEX,{"derivedFrom":[subQ7,subQ0]});Q8=makeQuery(id+"F0.imprint","IMPRINT",FACE,{"disambiguationData":[TD([[makeQuery(id+"F0.imprint","IMPRINT",EDGE,{"disambiguationData":[TD([[subQ9,-1.0]])],"derivedFrom":subQ7}),1.0]])]});}
            var Q9;
            {var subQ0=sQuery(id+"F0.wireOp",EDGE,"E8");var subQ1=sQuery(id+"F0.wireOp",EDGE,"E0");var subQ2=makeQuery(id+"F0.imprint","INTERSECT",VERTEX,{"derivedFrom":[subQ1,subQ0]});Q9=makeQuery(id+"F0.imprint","IMPRINT",FACE,{"disambiguationData":[TD([[makeQuery(id+"F0.imprint","IMPRINT",EDGE,{"disambiguationData":[TD([[subQ2,1.0]])],"derivedFrom":subQ1}),-1.0]])]});}
            var Q10;
            {var subQ0=sQuery(id+"F0.wireOp",EDGE,"E48.0");var subQ1=sQuery(id+"F0.wireOp",EDGE,"E0");var subQ2=makeQuery(id+"F0.imprint","INTERSECT",VERTEX,{"derivedFrom":[subQ1,subQ0]});Q10=makeQuery(id+"F0.imprint","IMPRINT",FACE,{"disambiguationData":[TD([[makeQuery(id+"F0.imprint","IMPRINT",EDGE,{"disambiguationData":[TD([[subQ2,-1.0]])],"derivedFrom":subQ1}),-1.0]])]});}
            var Q11;
            {var subQ0=sQuery(id+"F0.wireOp",EDGE,"E10");Q11=makeQuery(id+"F0.imprint","IMPRINT",FACE,{"disambiguationData":[TD([[makeQuery(id+"F0.imprint","IMPRINT",EDGE,{"derivedFrom":subQ0}),1.0]])]});}
            var Q12;
            {var subQ5=sQuery(id+"F0.wireOp",EDGE,"E30");var subQ7=sQuery(id+"F0.wireOp",EDGE,"E0");var subQ9=makeQuery(id+"F0.imprint","INTERSECT",VERTEX,{"derivedFrom":[subQ7,subQ5]});Q12=makeQuery(id+"F0.imprint","IMPRINT",FACE,{"disambiguationData":[TD([[makeQuery(id+"F0.imprint","IMPRINT",EDGE,{"disambiguationData":[TD([[subQ9,-1.0]])],"derivedFrom":subQ7}),1.0]])]});}
            var Q13;
            {var subQ0=sQuery(id+"F0.wireOp",EDGE,"E11");Q13=makeQuery(id+"F0.imprint","IMPRINT",FACE,{"disambiguationData":[TD([[makeQuery(id+"F0.imprint","IMPRINT",EDGE,{"derivedFrom":subQ0}),-1.0]])]});}
            var Q14;
            {var subQ0=sQuery(id+"F0.wireOp",EDGE,"E30");var subQ1=sQuery(id+"F0.wireOp",EDGE,"E0");var subQ2=makeQuery(id+"F0.imprint","INTERSECT",VERTEX,{"derivedFrom":[subQ1,subQ0]});Q14=makeQuery(id+"F0.imprint","IMPRINT",FACE,{"disambiguationData":[TD([[makeQuery(id+"F0.imprint","IMPRINT",EDGE,{"disambiguationData":[TD([[subQ2,-1.0]])],"derivedFrom":subQ1}),-1.0]])]});}
            var Q15;
            {var subQ0=sQuery(id+"F0.wireOp",EDGE,"E6");var subQ5=sQuery(id+"F0.wireOp",EDGE,"E7");var subQ6=makeQuery(id+"F0.imprint","INTERSECT",VERTEX,{"derivedFrom":[subQ0,subQ5]});Q15=makeQuery(id+"F0.imprint","IMPRINT",FACE,{"disambiguationData":[TD([[makeQuery(id+"F0.imprint","IMPRINT",EDGE,{"disambiguationData":[TD([[subQ6,1.0]])],"derivedFrom":subQ5}),-1.0]])]});}
            var Q16;
            {var subQ0=sQuery(id+"F0.wireOp",EDGE,"E29");var subQ1=sQuery(id+"F0.wireOp",EDGE,"E9");var subQ2=makeQuery(id+"F0.imprint","INTERSECT",VERTEX,{"derivedFrom":[subQ1,subQ0]});Q16=makeQuery(id+"F0.imprint","IMPRINT",FACE,{"disambiguationData":[TD([[makeQuery(id+"F0.imprint","IMPRINT",EDGE,{"disambiguationData":[TD([[subQ2,-1.0]])],"derivedFrom":subQ1}),-1.0]])]});}
            var Q17;
            {var subQ0=sQuery(id+"F0.wireOp",EDGE,"E30");var subQ1=sQuery(id+"F0.wireOp",EDGE,"E7");var subQ2=makeQuery(id+"F0.imprint","INTERSECT",VERTEX,{"derivedFrom":[subQ1,subQ0]});Q17=makeQuery(id+"F0.imprint","IMPRINT",FACE,{"disambiguationData":[TD([[makeQuery(id+"F0.imprint","IMPRINT",EDGE,{"disambiguationData":[TD([[subQ2,1.0]])],"derivedFrom":subQ1}),-1.0]])]});}
            var Q18;
            {var subQ0=sQuery(id+"F0.wireOp",EDGE,"E54.converted");var subQ1=sQuery(id+"F0.wireOp",EDGE,"E29");var subQ2=makeQuery(id+"F0.imprint","INTERSECT",VERTEX,{"derivedFrom":[subQ1,subQ0]});Q18=makeQuery(id+"F0.imprint","IMPRINT",FACE,{"disambiguationData":[TD([[makeQuery(id+"F0.imprint","IMPRINT",EDGE,{"disambiguationData":[TD([[subQ2,-1.0]])],"derivedFrom":subQ1}),-1.0]])]});}
            var Q19;
            {var subQ0=sQuery(id+"F0.wireOp",EDGE,"E54.converted");var subQ1=sQuery(id+"F0.wireOp",EDGE,"E30");var subQ2=makeQuery(id+"F0.imprint","INTERSECT",VERTEX,{"derivedFrom":[subQ1,subQ0]});Q19=makeQuery(id+"F0.imprint","IMPRINT",FACE,{"disambiguationData":[TD([[makeQuery(id+"F0.imprint","IMPRINT",EDGE,{"disambiguationData":[TD([[subQ2,-1.0]])],"derivedFrom":subQ1}),1.0]])]});}
            var Q20;
            {var subQ0=sQuery(id+"F0.wireOp",EDGE,"E53");var subQ1=sQuery(id+"F0.wireOp",EDGE,"E8");var subQ2=makeQuery(id+"F0.imprint","INTERSECT",VERTEX,{"derivedFrom":[subQ1,subQ0]});Q20=makeQuery(id+"F0.imprint","IMPRINT",FACE,{"disambiguationData":[TD([[makeQuery(id+"F0.imprint","IMPRINT",EDGE,{"disambiguationData":[TD([[subQ2,1.0]])],"derivedFrom":subQ1}),-1.0]])]});}
            var Q21;
            {var subQ0=sQuery(id+"F0.wireOp",EDGE,"E53");var subQ1=sQuery(id+"F0.wireOp",EDGE,"E6");var subQ2=makeQuery(id+"F0.imprint","INTERSECT",VERTEX,{"derivedFrom":[subQ1,subQ0]});Q21=makeQuery(id+"F0.imprint","IMPRINT",FACE,{"disambiguationData":[TD([[makeQuery(id+"F0.imprint","IMPRINT",EDGE,{"disambiguationData":[TD([[subQ2,1.0]])],"derivedFrom":subQ1}),1.0]])]});}
            var Q22;
            {var subQ1=sQuery(id+"F0.wireOp",EDGE,"E0");var subQ3=sQuery(id+"F0.wireOp",EDGE,"E30");var subQ4=makeQuery(id+"F0.imprint","INTERSECT",VERTEX,{"derivedFrom":[subQ1,subQ3]});Q22=makeQuery(id+"F0.imprint","IMPRINT",FACE,{"disambiguationData":[TD([[makeQuery(id+"F0.imprint","IMPRINT",EDGE,{"disambiguationData":[TD([[subQ4,-1.0]])],"derivedFrom":subQ3}),-1.0]])]});}
            var Q23;
            {var subQ0=sQuery(id+"F0.wireOp",EDGE,"E10");var subQ1=sQuery(id+"F0.wireOp",EDGE,"E0");var subQ2=makeQuery(id+"F0.imprint","INTERSECT",VERTEX,{"derivedFrom":[subQ1,subQ0]});Q23=makeQuery(id+"F0.imprint","IMPRINT",FACE,{"disambiguationData":[TD([[makeQuery(id+"F0.imprint","IMPRINT",EDGE,{"disambiguationData":[TD([[subQ2,1.0]])],"derivedFrom":subQ1}),-1.0]])]});}
            var Q24;
            {var subQ0=sQuery(id+"F0.wireOp",EDGE,"E53");var subQ1=sQuery(id+"F0.wireOp",EDGE,"E10");var subQ2=makeQuery(id+"F0.imprint","INTERSECT",VERTEX,{"derivedFrom":[subQ1,subQ0]});Q24=makeQuery(id+"F0.imprint","IMPRINT",FACE,{"disambiguationData":[TD([[makeQuery(id+"F0.imprint","IMPRINT",EDGE,{"disambiguationData":[TD([[subQ2,1.0]])],"derivedFrom":subQ1}),-1.0]])]});}
            var Q25;
            {var subQ0=sQuery(id+"F0.wireOp",EDGE,"E53");var subQ1=sQuery(id+"F0.wireOp",EDGE,"E6");var subQ2=makeQuery(id+"F0.imprint","INTERSECT",VERTEX,{"derivedFrom":[subQ1,subQ0]});Q25=makeQuery(id+"F0.imprint","IMPRINT",FACE,{"disambiguationData":[TD([[makeQuery(id+"F0.imprint","IMPRINT",EDGE,{"disambiguationData":[TD([[subQ2,1.0]])],"derivedFrom":subQ1}),-1.0]])]});}
            extrude(context, id + "F5", {"entities" : qUnion([Q0, Q1, Q2, Q3, Q4, Q5, Q6, Q7, Q8, Q9, Q10, Q11, Q12, Q13, Q14, Q15, Q16, Q17, Q18, Q19, Q20, Q21, Q22, Q23, Q24, Q25]), "operationType" : NewBodyOperationType.ADD, "depth" : 38.1 * mm, "offsetDistance" : 25.4 * mm, "hasSecondDirection" : true, "secondDirectionOppositeDirection" : false, "secondDirectionDepth" : 34.92 * mm});
        }
        {
            var Q0;
            {var subQ0=sQuery(id+"F0.wireOp",EDGE,"E48.0");var subQ1=sQuery(id+"F0.wireOp",EDGE,"E0");var subQ2=makeQuery(id+"F0.imprint","INTERSECT",VERTEX,{"derivedFrom":[subQ1,subQ0]});Q0=makeQuery(id+"F0.imprint","IMPRINT",FACE,{"disambiguationData":[TD([[makeQuery(id+"F0.imprint","IMPRINT",EDGE,{"disambiguationData":[TD([[subQ2,-1.0]])],"derivedFrom":subQ1}),-1.0]])]});}
            var Q1;
            {var subQ0=sQuery(id+"F0.wireOp",EDGE,"E11");Q1=makeQuery(id+"F0.imprint","IMPRINT",FACE,{"disambiguationData":[TD([[makeQuery(id+"F0.imprint","IMPRINT",EDGE,{"derivedFrom":subQ0}),-1.0]])]});}
            var Q2;
            {var subQ0=sQuery(id+"F0.wireOp",EDGE,"E51.2.1");Q2=makeQuery(id+"F0.imprint","IMPRINT",FACE,{"disambiguationData":[TD([[makeQuery(id+"F0.imprint","IMPRINT",EDGE,{"derivedFrom":subQ0}),1.0]])]});}
            var Q3;
            {var subQ5=sQuery(id+"F0.wireOp",EDGE,"E30");var subQ7=sQuery(id+"F0.wireOp",EDGE,"E0");var subQ9=makeQuery(id+"F0.imprint","INTERSECT",VERTEX,{"derivedFrom":[subQ7,subQ5]});Q3=makeQuery(id+"F0.imprint","IMPRINT",FACE,{"disambiguationData":[TD([[makeQuery(id+"F0.imprint","IMPRINT",EDGE,{"disambiguationData":[TD([[subQ9,-1.0]])],"derivedFrom":subQ7}),1.0]])]});}
            var Q4;
            {var subQ0=sQuery(id+"F0.wireOp",EDGE,"E51.6.1");Q4=makeQuery(id+"F0.imprint","IMPRINT",FACE,{"disambiguationData":[TD([[makeQuery(id+"F0.imprint","IMPRINT",EDGE,{"derivedFrom":subQ0}),1.0]])]});}
            var Q5;
            {var subQ0=sQuery(id+"F0.wireOp",EDGE,"E6");var subQ5=sQuery(id+"F0.wireOp",EDGE,"E7");var subQ6=makeQuery(id+"F0.imprint","INTERSECT",VERTEX,{"derivedFrom":[subQ0,subQ5]});Q5=makeQuery(id+"F0.imprint","IMPRINT",FACE,{"disambiguationData":[TD([[makeQuery(id+"F0.imprint","IMPRINT",EDGE,{"disambiguationData":[TD([[subQ6,1.0]])],"derivedFrom":subQ5}),-1.0]])]});}
            var Q6;
            {var subQ0=sQuery(id+"F0.wireOp",EDGE,"E51.5.1");Q6=makeQuery(id+"F0.imprint","IMPRINT",FACE,{"disambiguationData":[TD([[makeQuery(id+"F0.imprint","IMPRINT",EDGE,{"derivedFrom":subQ0}),1.0]])]});}
            var Q7;
            {var subQ0=sQuery(id+"F0.wireOp",EDGE,"E51.1.1");Q7=makeQuery(id+"F0.imprint","IMPRINT",FACE,{"disambiguationData":[TD([[makeQuery(id+"F0.imprint","IMPRINT",EDGE,{"derivedFrom":subQ0}),1.0]])]});}
            var Q8;
            {var subQ0=sQuery(id+"F0.wireOp",EDGE,"E30");var subQ1=sQuery(id+"F0.wireOp",EDGE,"E0");var subQ2=makeQuery(id+"F0.imprint","INTERSECT",VERTEX,{"derivedFrom":[subQ1,subQ0]});Q8=makeQuery(id+"F0.imprint","IMPRINT",FACE,{"disambiguationData":[TD([[makeQuery(id+"F0.imprint","IMPRINT",EDGE,{"disambiguationData":[TD([[subQ2,-1.0]])],"derivedFrom":subQ1}),-1.0]])]});}
            var Q9;
            {var subQ5=sQuery(id+"F0.wireOp",EDGE,"E5.8.1");Q9=makeQuery(id+"F0.imprint","IMPRINT",FACE,{"disambiguationData":[TD([[makeQuery(id+"F0.imprint","IMPRINT",EDGE,{"derivedFrom":subQ5}),-1.0]])]});}
            var Q10;
            {var subQ0=sQuery(id+"F0.wireOp",EDGE,"E8");var subQ1=sQuery(id+"F0.wireOp",EDGE,"E0");var subQ2=makeQuery(id+"F0.imprint","INTERSECT",VERTEX,{"derivedFrom":[subQ1,subQ0]});Q10=makeQuery(id+"F0.imprint","IMPRINT",FACE,{"disambiguationData":[TD([[makeQuery(id+"F0.imprint","IMPRINT",EDGE,{"disambiguationData":[TD([[subQ2,1.0]])],"derivedFrom":subQ1}),-1.0]])]});}
            var Q11;
            {var subQ0=sQuery(id+"F0.wireOp",EDGE,"E10");Q11=makeQuery(id+"F0.imprint","IMPRINT",FACE,{"disambiguationData":[TD([[makeQuery(id+"F0.imprint","IMPRINT",EDGE,{"derivedFrom":subQ0}),1.0]])]});}
            var Q12;
            {var subQ23=sQuery(id+"F0.wireOp",EDGE,"E3.0");Q12=makeQuery(id+"F0.imprint","IMPRINT",FACE,{"disambiguationData":[TD([[makeQuery(id+"F0.imprint","IMPRINT",EDGE,{"derivedFrom":subQ23}),1.0]])]});}
            var Q13;
            {var subQ0=sQuery(id+"F0.wireOp",EDGE,"E48.0");var subQ7=sQuery(id+"F0.wireOp",EDGE,"E0");var subQ9=makeQuery(id+"F0.imprint","INTERSECT",VERTEX,{"derivedFrom":[subQ7,subQ0]});Q13=makeQuery(id+"F0.imprint","IMPRINT",FACE,{"disambiguationData":[TD([[makeQuery(id+"F0.imprint","IMPRINT",EDGE,{"disambiguationData":[TD([[subQ9,-1.0]])],"derivedFrom":subQ7}),1.0]])]});}
            var Q14;
            {var subQ0=sQuery(id+"F0.wireOp",EDGE,"E30");var subQ1=sQuery(id+"F0.wireOp",EDGE,"E7");var subQ2=makeQuery(id+"F0.imprint","INTERSECT",VERTEX,{"derivedFrom":[subQ1,subQ0]});Q14=makeQuery(id+"F0.imprint","IMPRINT",FACE,{"disambiguationData":[TD([[makeQuery(id+"F0.imprint","IMPRINT",EDGE,{"disambiguationData":[TD([[subQ2,1.0]])],"derivedFrom":subQ1}),-1.0]])]});}
            var Q15;
            {var subQ0=sQuery(id+"F0.wireOp",EDGE,"E29");var subQ1=sQuery(id+"F0.wireOp",EDGE,"E9");var subQ2=makeQuery(id+"F0.imprint","INTERSECT",VERTEX,{"derivedFrom":[subQ1,subQ0]});Q15=makeQuery(id+"F0.imprint","IMPRINT",FACE,{"disambiguationData":[TD([[makeQuery(id+"F0.imprint","IMPRINT",EDGE,{"disambiguationData":[TD([[subQ2,-1.0]])],"derivedFrom":subQ1}),-1.0]])]});}
            var Q16;
            {var subQ1=sQuery(id+"F0.wireOp",EDGE,"E0");var subQ3=sQuery(id+"F0.wireOp",EDGE,"E30");var subQ4=makeQuery(id+"F0.imprint","INTERSECT",VERTEX,{"derivedFrom":[subQ1,subQ3]});Q16=makeQuery(id+"F0.imprint","IMPRINT",FACE,{"disambiguationData":[TD([[makeQuery(id+"F0.imprint","IMPRINT",EDGE,{"disambiguationData":[TD([[subQ4,-1.0]])],"derivedFrom":subQ3}),-1.0]])]});}
            var Q17;
            {var subQ0=sQuery(id+"F0.wireOp",EDGE,"E53");var subQ1=sQuery(id+"F0.wireOp",EDGE,"E6");var subQ2=makeQuery(id+"F0.imprint","INTERSECT",VERTEX,{"derivedFrom":[subQ1,subQ0]});Q17=makeQuery(id+"F0.imprint","IMPRINT",FACE,{"disambiguationData":[TD([[makeQuery(id+"F0.imprint","IMPRINT",EDGE,{"disambiguationData":[TD([[subQ2,1.0]])],"derivedFrom":subQ1}),1.0]])]});}
            var Q18;
            {var subQ0=sQuery(id+"F0.wireOp",EDGE,"E54.converted");var subQ1=sQuery(id+"F0.wireOp",EDGE,"E30");var subQ2=makeQuery(id+"F0.imprint","INTERSECT",VERTEX,{"derivedFrom":[subQ1,subQ0]});Q18=makeQuery(id+"F0.imprint","IMPRINT",FACE,{"disambiguationData":[TD([[makeQuery(id+"F0.imprint","IMPRINT",EDGE,{"disambiguationData":[TD([[subQ2,-1.0]])],"derivedFrom":subQ1}),1.0]])]});}
            var Q19;
            {var subQ0=sQuery(id+"F0.wireOp",EDGE,"E10");var subQ1=sQuery(id+"F0.wireOp",EDGE,"E0");var subQ2=makeQuery(id+"F0.imprint","INTERSECT",VERTEX,{"derivedFrom":[subQ1,subQ0]});Q19=makeQuery(id+"F0.imprint","IMPRINT",FACE,{"disambiguationData":[TD([[makeQuery(id+"F0.imprint","IMPRINT",EDGE,{"disambiguationData":[TD([[subQ2,1.0]])],"derivedFrom":subQ1}),-1.0]])]});}
            var Q20;
            {var subQ0=sQuery(id+"F0.wireOp",EDGE,"E53");var subQ1=sQuery(id+"F0.wireOp",EDGE,"E10");var subQ2=makeQuery(id+"F0.imprint","INTERSECT",VERTEX,{"derivedFrom":[subQ1,subQ0]});Q20=makeQuery(id+"F0.imprint","IMPRINT",FACE,{"disambiguationData":[TD([[makeQuery(id+"F0.imprint","IMPRINT",EDGE,{"disambiguationData":[TD([[subQ2,1.0]])],"derivedFrom":subQ1}),-1.0]])]});}
            var Q21;
            {var subQ0=sQuery(id+"F0.wireOp",EDGE,"E54.converted");var subQ1=sQuery(id+"F0.wireOp",EDGE,"E29");var subQ2=makeQuery(id+"F0.imprint","INTERSECT",VERTEX,{"derivedFrom":[subQ1,subQ0]});Q21=makeQuery(id+"F0.imprint","IMPRINT",FACE,{"disambiguationData":[TD([[makeQuery(id+"F0.imprint","IMPRINT",EDGE,{"disambiguationData":[TD([[subQ2,-1.0]])],"derivedFrom":subQ1}),-1.0]])]});}
            var Q22;
            {var subQ0=sQuery(id+"F0.wireOp",EDGE,"E53");var subQ1=sQuery(id+"F0.wireOp",EDGE,"E8");var subQ2=makeQuery(id+"F0.imprint","INTERSECT",VERTEX,{"derivedFrom":[subQ1,subQ0]});Q22=makeQuery(id+"F0.imprint","IMPRINT",FACE,{"disambiguationData":[TD([[makeQuery(id+"F0.imprint","IMPRINT",EDGE,{"disambiguationData":[TD([[subQ2,1.0]])],"derivedFrom":subQ1}),-1.0]])]});}
            var Q23;
            {var subQ0=sQuery(id+"F0.wireOp",EDGE,"E13.trimOffspring");Q23=makeQuery(id+"F0.imprint","IMPRINT",FACE,{"disambiguationData":[TD([[makeQuery(id+"F0.imprint","IMPRINT",EDGE,{"derivedFrom":subQ0}),-1.0]])]});}
            var Q24;
            {var subQ0=sQuery(id+"F0.wireOp",EDGE,"E53");var subQ1=sQuery(id+"F0.wireOp",EDGE,"E6");var subQ2=makeQuery(id+"F0.imprint","INTERSECT",VERTEX,{"derivedFrom":[subQ1,subQ0]});Q24=makeQuery(id+"F0.imprint","IMPRINT",FACE,{"disambiguationData":[TD([[makeQuery(id+"F0.imprint","IMPRINT",EDGE,{"disambiguationData":[TD([[subQ2,1.0]])],"derivedFrom":subQ1}),-1.0]])]});}
            var Q25;
            {var subQ0=sQuery(id+"F0.wireOp",EDGE,"E9");var subQ1=sQuery(id+"F0.wireOp",EDGE,"E8");var subQ2=makeQuery(id+"F0.imprint","INTERSECT",VERTEX,{"derivedFrom":[subQ1,subQ0]});Q25=makeQuery(id+"F0.imprint","IMPRINT",FACE,{"disambiguationData":[TD([[makeQuery(id+"F0.imprint","IMPRINT",EDGE,{"disambiguationData":[TD([[subQ2,1.0]])],"derivedFrom":subQ1}),-1.0]])]});}
            extrude(context, id + "F6", {"entities" : qUnion([Q0, Q1, Q2, Q3, Q4, Q5, Q6, Q7, Q8, Q9, Q10, Q11, Q12, Q13, Q14, Q15, Q16, Q17, Q18, Q19, Q20, Q21, Q22, Q23, Q24, Q25]), "operationType" : NewBodyOperationType.ADD, "oppositeDirection" : true, "depth" : 38.1 * mm, "offsetDistance" : 25.4 * mm, "hasSecondDirection" : true, "secondDirectionOppositeDirection" : true, "secondDirectionDepth" : 34.92 * mm});
        }
        {
            var Q0;
            {var subQ0=sQuery(id+"F0.wireOp",EDGE,"E54.converted");var subQ1=sQuery(id+"F0.wireOp",EDGE,"E29");var subQ2=makeQuery(id+"F0.imprint","INTERSECT",VERTEX,{"derivedFrom":[subQ1,subQ0]});Q0=makeQuery(id+"F0.imprint","IMPRINT",FACE,{"disambiguationData":[TD([[makeQuery(id+"F0.imprint","IMPRINT",EDGE,{"disambiguationData":[TD([[subQ2,-1.0]])],"derivedFrom":subQ1}),-1.0]])]});}
            var Q1;
            {var subQ0=sQuery(id+"F0.wireOp",EDGE,"E53");var subQ1=sQuery(id+"F0.wireOp",EDGE,"E8");var subQ2=makeQuery(id+"F0.imprint","INTERSECT",VERTEX,{"derivedFrom":[subQ1,subQ0]});Q1=makeQuery(id+"F0.imprint","IMPRINT",FACE,{"disambiguationData":[TD([[makeQuery(id+"F0.imprint","IMPRINT",EDGE,{"disambiguationData":[TD([[subQ2,1.0]])],"derivedFrom":subQ1}),-1.0]])]});}
            var Q2;
            {var subQ0=sQuery(id+"F0.wireOp",EDGE,"E53");var subQ1=sQuery(id+"F0.wireOp",EDGE,"E6");var subQ2=makeQuery(id+"F0.imprint","INTERSECT",VERTEX,{"derivedFrom":[subQ1,subQ0]});Q2=makeQuery(id+"F0.imprint","IMPRINT",FACE,{"disambiguationData":[TD([[makeQuery(id+"F0.imprint","IMPRINT",EDGE,{"disambiguationData":[TD([[subQ2,1.0]])],"derivedFrom":subQ1}),1.0]])]});}
            var Q3;
            {var subQ0=sQuery(id+"F0.wireOp",EDGE,"E53");var subQ1=sQuery(id+"F0.wireOp",EDGE,"E11");var subQ2=makeQuery(id+"F0.imprint","INTERSECT",VERTEX,{"derivedFrom":[subQ1,subQ0]});Q3=makeQuery(id+"F0.imprint","IMPRINT",FACE,{"disambiguationData":[TD([[makeQuery(id+"F0.imprint","IMPRINT",EDGE,{"disambiguationData":[TD([[subQ2,1.0]])],"derivedFrom":subQ1}),-1.0]])]});}
            var Q4;
            {var subQ0=sQuery(id+"F0.wireOp",EDGE,"E53");var subQ1=sQuery(id+"F0.wireOp",EDGE,"E10");var subQ2=makeQuery(id+"F0.imprint","INTERSECT",VERTEX,{"derivedFrom":[subQ1,subQ0]});Q4=makeQuery(id+"F0.imprint","IMPRINT",FACE,{"disambiguationData":[TD([[makeQuery(id+"F0.imprint","IMPRINT",EDGE,{"disambiguationData":[TD([[subQ2,1.0]])],"derivedFrom":subQ1}),1.0]])]});}
            var Q5;
            {var subQ0=sQuery(id+"F0.wireOp",EDGE,"E54.converted");var subQ1=sQuery(id+"F0.wireOp",EDGE,"E30");var subQ2=makeQuery(id+"F0.imprint","INTERSECT",VERTEX,{"derivedFrom":[subQ1,subQ0]});Q5=makeQuery(id+"F0.imprint","IMPRINT",FACE,{"disambiguationData":[TD([[makeQuery(id+"F0.imprint","IMPRINT",EDGE,{"disambiguationData":[TD([[subQ2,-1.0]])],"derivedFrom":subQ1}),1.0]])]});}
            var Q6;
            {var subQ0=sQuery(id+"F0.wireOp",EDGE,"E53");var subQ1=sQuery(id+"F0.wireOp",EDGE,"E10");var subQ2=makeQuery(id+"F0.imprint","INTERSECT",VERTEX,{"derivedFrom":[subQ1,subQ0]});Q6=makeQuery(id+"F0.imprint","IMPRINT",FACE,{"disambiguationData":[TD([[makeQuery(id+"F0.imprint","IMPRINT",EDGE,{"disambiguationData":[TD([[subQ2,1.0]])],"derivedFrom":subQ1}),-1.0]])]});}
            var Q7;
            {var subQ0=sQuery(id+"F0.wireOp",EDGE,"E53");var subQ1=sQuery(id+"F0.wireOp",EDGE,"E6");var subQ2=makeQuery(id+"F0.imprint","INTERSECT",VERTEX,{"derivedFrom":[subQ1,subQ0]});Q7=makeQuery(id+"F0.imprint","IMPRINT",FACE,{"disambiguationData":[TD([[makeQuery(id+"F0.imprint","IMPRINT",EDGE,{"disambiguationData":[TD([[subQ2,1.0]])],"derivedFrom":subQ1}),-1.0]])]});}
            extrude(context, id + "F7", {"entities" : qUnion([Q0, Q1, Q2, Q3, Q4, Q5, Q6, Q7]), "operationType" : NewBodyOperationType.ADD, "oppositeDirection" : true, "depth" : 1022.35 * mm, "offsetDistance" : 25.4 * mm, "hasSecondDirection" : true, "secondDirectionOppositeDirection" : true, "secondDirectionDepth" : 38.1 * mm});
        }
        {
            var Q0;
            {var subQ17=sQuery(id+"F1.wireOp",EDGE,"E58.4.0");var subQ19=sQuery(id+"F1.wireOp",EDGE,"E55");var subQ20=makeQuery(id+"F1.imprint","INTERSECT",VERTEX,{"derivedFrom":[subQ19,subQ17]});Q0=makeQuery(id+"F1.imprint","IMPRINT",FACE,{"disambiguationData":[TD([[makeQuery(id+"F1.imprint","IMPRINT",EDGE,{"disambiguationData":[TD([[subQ20,-1.0]])],"derivedFrom":subQ19}),1.0]])]});}
            var Q1;
            {var subQ5=sQuery(id+"F1.wireOp",EDGE,"E58.4.0");var subQ7=sQuery(id+"F1.wireOp",EDGE,"E55");var subQ8=makeQuery(id+"F1.imprint","INTERSECT",VERTEX,{"derivedFrom":[subQ7,subQ5]});Q1=makeQuery(id+"F1.imprint","IMPRINT",FACE,{"disambiguationData":[TD([[makeQuery(id+"F1.imprint","IMPRINT",EDGE,{"disambiguationData":[TD([[subQ8,1.0]])],"derivedFrom":subQ7}),1.0]])]});}
            extrude(context, id + "F8", {"entities" : qUnion([Q0, Q1]), "operationType" : NewBodyOperationType.ADD, "oppositeDirection" : true, "depth" : 1016 * mm, "offsetDistance" : 25.4 * mm, "hasSecondDirection" : true, "secondDirectionOppositeDirection" : true, "secondDirectionDepth" : 609.6 * mm});
        }
        {
            var Q0;
            Q0=makeQuery(id+"F1.imprint","IMPRINT",FACE,{"disambiguationData":[TD([[makeQuery(id+"F1.imprint","IMPRINT",EDGE,{"derivedFrom":sQuery(id+"F1.wireOp",EDGE,"E56")}),-1.0]])]});
            extrude(context, id + "F9", {"entities" : qUnion([Q0]), "oppositeDirection" : true, "depth" : 1168.4 * mm, "offsetDistance" : 25.4 * mm, "hasSecondDirection" : true, "secondDirectionOppositeDirection" : true, "secondDirectionDepth" : 1092.2 * mm});
        }
        {
            var Q0;
            Q0=makeQuery(id+"F2.imprint","IMPRINT",FACE,{"disambiguationData":[TD([[makeQuery(id+"F2.imprint","IMPRINT",EDGE,{"derivedFrom":sQuery(id+"F2.wireOp",EDGE,"E105")}),1.0]])]});
            extrude(context, id + "F10", {"entities" : qUnion([Q0]), "operationType" : NewBodyOperationType.REMOVE, "oppositeDirection" : true, "depth" : 889 * mm, "offsetDistance" : 25.4 * mm, "hasDraft" : true, "draftAngle" : 4 * degree, "hasSecondDirection" : true, "secondDirectionOppositeDirection" : true, "secondDirectionDepth" : 50.8 * mm});
        }
        {
            var Q0;
            Q0=makeQuery(id+"F1.imprint","IMPRINT",FACE,{"disambiguationData":[TD([[makeQuery(id+"F1.imprint","IMPRINT",EDGE,{"derivedFrom":sQuery(id+"F1.wireOp",EDGE,"E56")}),-1.0]])]});
            var Q1;
            {var subQ0=sQuery(id+"F1.wireOp",EDGE,"E59.converted");var subQ1=sQuery(id+"F1.wireOp",EDGE,"E58.10.0");var subQ2=makeQuery(id+"F1.imprint","INTERSECT",VERTEX,{"derivedFrom":[subQ1,subQ0]});Q1=makeQuery(id+"F1.imprint","IMPRINT",FACE,{"disambiguationData":[TD([[makeQuery(id+"F1.imprint","IMPRINT",EDGE,{"disambiguationData":[TD([[subQ2,-1.0]])],"derivedFrom":subQ1}),-1.0]])]});}
            var Q2;
            {var subQ0=sQuery(id+"F1.wireOp",EDGE,"E59.converted");var subQ1=sQuery(id+"F1.wireOp",EDGE,"E58.4.1");var subQ2=makeQuery(id+"F1.imprint","INTERSECT",VERTEX,{"derivedFrom":[subQ1,subQ0]});Q2=makeQuery(id+"F1.imprint","IMPRINT",FACE,{"disambiguationData":[TD([[makeQuery(id+"F1.imprint","IMPRINT",EDGE,{"disambiguationData":[TD([[subQ2,-1.0]])],"derivedFrom":subQ1}),1.0]])]});}
            var Q3;
            {var subQ0=sQuery(id+"F1.wireOp",EDGE,"E59.converted");var subQ1=sQuery(id+"F1.wireOp",EDGE,"E58.6.0");var subQ2=makeQuery(id+"F1.imprint","INTERSECT",VERTEX,{"derivedFrom":[subQ1,subQ0]});Q3=makeQuery(id+"F1.imprint","IMPRINT",FACE,{"disambiguationData":[TD([[makeQuery(id+"F1.imprint","IMPRINT",EDGE,{"disambiguationData":[TD([[subQ2,-1.0]])],"derivedFrom":subQ1}),1.0]])]});}
            var Q4;
            {var subQ0=sQuery(id+"F1.wireOp",EDGE,"E64");var subQ1=sQuery(id+"F1.wireOp",EDGE,"E58.11.1");var subQ2=makeQuery(id+"F1.imprint","INTERSECT",VERTEX,{"derivedFrom":[subQ1,subQ0]});Q4=makeQuery(id+"F1.imprint","IMPRINT",FACE,{"disambiguationData":[TD([[makeQuery(id+"F1.imprint","IMPRINT",EDGE,{"disambiguationData":[TD([[subQ2,-1.0]])],"derivedFrom":subQ1}),1.0]])]});}
            var Q5;
            {var subQ0=sQuery(id+"F1.wireOp",EDGE,"E59.converted");var subQ1=sQuery(id+"F1.wireOp",EDGE,"E58.7.0");var subQ2=makeQuery(id+"F1.imprint","INTERSECT",VERTEX,{"derivedFrom":[subQ1,subQ0]});Q5=makeQuery(id+"F1.imprint","IMPRINT",FACE,{"disambiguationData":[TD([[makeQuery(id+"F1.imprint","IMPRINT",EDGE,{"disambiguationData":[TD([[subQ2,-1.0]])],"derivedFrom":subQ1}),1.0]])]});}
            var Q6;
            {var subQ0=sQuery(id+"F1.wireOp",EDGE,"E59.converted");var subQ1=sQuery(id+"F1.wireOp",EDGE,"E58.4.2");var subQ2=makeQuery(id+"F1.imprint","INTERSECT",VERTEX,{"derivedFrom":[subQ1,subQ0]});Q6=makeQuery(id+"F1.imprint","IMPRINT",FACE,{"disambiguationData":[TD([[makeQuery(id+"F1.imprint","IMPRINT",EDGE,{"disambiguationData":[TD([[subQ2,-1.0]])],"derivedFrom":subQ1}),-1.0]])]});}
            var Q7;
            {var subQ0=sQuery(id+"F1.wireOp",EDGE,"E64");var subQ1=sQuery(id+"F1.wireOp",EDGE,"E58.9.0");var subQ2=makeQuery(id+"F1.imprint","INTERSECT",VERTEX,{"derivedFrom":[subQ1,subQ0]});Q7=makeQuery(id+"F1.imprint","IMPRINT",FACE,{"disambiguationData":[TD([[makeQuery(id+"F1.imprint","IMPRINT",EDGE,{"disambiguationData":[TD([[subQ2,-1.0]])],"derivedFrom":subQ1}),1.0]])]});}
            var Q8;
            {var subQ0=sQuery(id+"F1.wireOp",EDGE,"E64");var subQ1=sQuery(id+"F1.wireOp",EDGE,"E58.12.0");var subQ2=makeQuery(id+"F1.imprint","INTERSECT",VERTEX,{"derivedFrom":[subQ1,subQ0]});Q8=makeQuery(id+"F1.imprint","IMPRINT",FACE,{"disambiguationData":[TD([[makeQuery(id+"F1.imprint","IMPRINT",EDGE,{"disambiguationData":[TD([[subQ2,-1.0]])],"derivedFrom":subQ1}),1.0]])]});}
            var Q9;
            {var subQ0=sQuery(id+"F1.wireOp",EDGE,"E64");var subQ1=sQuery(id+"F1.wireOp",EDGE,"E58.5.0");var subQ2=makeQuery(id+"F1.imprint","INTERSECT",VERTEX,{"derivedFrom":[subQ1,subQ0]});Q9=makeQuery(id+"F1.imprint","IMPRINT",FACE,{"disambiguationData":[TD([[makeQuery(id+"F1.imprint","IMPRINT",EDGE,{"disambiguationData":[TD([[subQ2,-1.0]])],"derivedFrom":subQ1}),-1.0]])]});}
            var Q10;
            {var subQ0=sQuery(id+"F1.wireOp",EDGE,"E64");var subQ1=sQuery(id+"F1.wireOp",EDGE,"E58.4.1");var subQ2=makeQuery(id+"F1.imprint","INTERSECT",VERTEX,{"derivedFrom":[subQ1,subQ0]});Q10=makeQuery(id+"F1.imprint","IMPRINT",FACE,{"disambiguationData":[TD([[makeQuery(id+"F1.imprint","IMPRINT",EDGE,{"disambiguationData":[TD([[subQ2,-1.0]])],"derivedFrom":subQ1}),1.0]])]});}
            var Q11;
            {var subQ0=sQuery(id+"F1.wireOp",EDGE,"E59.converted");var subQ1=sQuery(id+"F1.wireOp",EDGE,"E58.7.1");var subQ2=makeQuery(id+"F1.imprint","INTERSECT",VERTEX,{"derivedFrom":[subQ1,subQ0]});Q11=makeQuery(id+"F1.imprint","IMPRINT",FACE,{"disambiguationData":[TD([[makeQuery(id+"F1.imprint","IMPRINT",EDGE,{"disambiguationData":[TD([[subQ2,-1.0]])],"derivedFrom":subQ1}),1.0]])]});}
            var Q12;
            {var subQ0=sQuery(id+"F1.wireOp",EDGE,"E59.converted");var subQ1=sQuery(id+"F1.wireOp",EDGE,"E58.8.1");var subQ2=makeQuery(id+"F1.imprint","INTERSECT",VERTEX,{"derivedFrom":[subQ1,subQ0]});Q12=makeQuery(id+"F1.imprint","IMPRINT",FACE,{"disambiguationData":[TD([[makeQuery(id+"F1.imprint","IMPRINT",EDGE,{"disambiguationData":[TD([[subQ2,-1.0]])],"derivedFrom":subQ1}),1.0]])]});}
            var Q13;
            {var subQ0=sQuery(id+"F1.wireOp",EDGE,"E59.converted");var subQ1=sQuery(id+"F1.wireOp",EDGE,"E58.7.0");var subQ2=makeQuery(id+"F1.imprint","INTERSECT",VERTEX,{"derivedFrom":[subQ1,subQ0]});Q13=makeQuery(id+"F1.imprint","IMPRINT",FACE,{"disambiguationData":[TD([[makeQuery(id+"F1.imprint","IMPRINT",EDGE,{"disambiguationData":[TD([[subQ2,-1.0]])],"derivedFrom":subQ1}),-1.0]])]});}
            var Q14;
            {var subQ0=sQuery(id+"F1.wireOp",EDGE,"E64");var subQ1=sQuery(id+"F1.wireOp",EDGE,"E58.9.0");var subQ2=makeQuery(id+"F1.imprint","INTERSECT",VERTEX,{"derivedFrom":[subQ1,subQ0]});Q14=makeQuery(id+"F1.imprint","IMPRINT",FACE,{"disambiguationData":[TD([[makeQuery(id+"F1.imprint","IMPRINT",EDGE,{"disambiguationData":[TD([[subQ2,-1.0]])],"derivedFrom":subQ1}),-1.0]])]});}
            var Q15;
            {var subQ0=sQuery(id+"F1.wireOp",EDGE,"E64");var subQ1=sQuery(id+"F1.wireOp",EDGE,"E58.10.0");var subQ2=makeQuery(id+"F1.imprint","INTERSECT",VERTEX,{"derivedFrom":[subQ1,subQ0]});Q15=makeQuery(id+"F1.imprint","IMPRINT",FACE,{"disambiguationData":[TD([[makeQuery(id+"F1.imprint","IMPRINT",EDGE,{"disambiguationData":[TD([[subQ2,-1.0]])],"derivedFrom":subQ1}),-1.0]])]});}
            var Q16;
            {var subQ0=sQuery(id+"F1.wireOp",EDGE,"E59.converted");var subQ1=sQuery(id+"F1.wireOp",EDGE,"E58.6.0");var subQ2=makeQuery(id+"F1.imprint","INTERSECT",VERTEX,{"derivedFrom":[subQ1,subQ0]});Q16=makeQuery(id+"F1.imprint","IMPRINT",FACE,{"disambiguationData":[TD([[makeQuery(id+"F1.imprint","IMPRINT",EDGE,{"disambiguationData":[TD([[subQ2,-1.0]])],"derivedFrom":subQ1}),-1.0]])]});}
            var Q17;
            {var subQ0=sQuery(id+"F1.wireOp",EDGE,"E64");var subQ1=sQuery(id+"F1.wireOp",EDGE,"E58.10.1");var subQ2=makeQuery(id+"F1.imprint","INTERSECT",VERTEX,{"derivedFrom":[subQ1,subQ0]});Q17=makeQuery(id+"F1.imprint","IMPRINT",FACE,{"disambiguationData":[TD([[makeQuery(id+"F1.imprint","IMPRINT",EDGE,{"disambiguationData":[TD([[subQ2,-1.0]])],"derivedFrom":subQ1}),1.0]])]});}
            var Q18;
            {var subQ0=sQuery(id+"F1.wireOp",EDGE,"E64");var subQ1=sQuery(id+"F1.wireOp",EDGE,"E58.11.0");var subQ2=makeQuery(id+"F1.imprint","INTERSECT",VERTEX,{"derivedFrom":[subQ1,subQ0]});Q18=makeQuery(id+"F1.imprint","IMPRINT",FACE,{"disambiguationData":[TD([[makeQuery(id+"F1.imprint","IMPRINT",EDGE,{"disambiguationData":[TD([[subQ2,-1.0]])],"derivedFrom":subQ1}),1.0]])]});}
            var Q19;
            {var subQ0=sQuery(id+"F1.wireOp",EDGE,"E64");var subQ1=sQuery(id+"F1.wireOp",EDGE,"E58.12.0");var subQ2=makeQuery(id+"F1.imprint","INTERSECT",VERTEX,{"derivedFrom":[subQ1,subQ0]});Q19=makeQuery(id+"F1.imprint","IMPRINT",FACE,{"disambiguationData":[TD([[makeQuery(id+"F1.imprint","IMPRINT",EDGE,{"disambiguationData":[TD([[subQ2,-1.0]])],"derivedFrom":subQ1}),-1.0]])]});}
            var Q20;
            {var subQ0=sQuery(id+"F1.wireOp",EDGE,"E59.converted");var subQ1=sQuery(id+"F1.wireOp",EDGE,"E58.9.0");var subQ2=makeQuery(id+"F1.imprint","INTERSECT",VERTEX,{"derivedFrom":[subQ1,subQ0]});Q20=makeQuery(id+"F1.imprint","IMPRINT",FACE,{"disambiguationData":[TD([[makeQuery(id+"F1.imprint","IMPRINT",EDGE,{"disambiguationData":[TD([[subQ2,-1.0]])],"derivedFrom":subQ1}),-1.0]])]});}
            var Q21;
            {var subQ0=sQuery(id+"F1.wireOp",EDGE,"E59.converted");var subQ1=sQuery(id+"F1.wireOp",EDGE,"E58.10.1");var subQ2=makeQuery(id+"F1.imprint","INTERSECT",VERTEX,{"derivedFrom":[subQ1,subQ0]});Q21=makeQuery(id+"F1.imprint","IMPRINT",FACE,{"disambiguationData":[TD([[makeQuery(id+"F1.imprint","IMPRINT",EDGE,{"disambiguationData":[TD([[subQ2,-1.0]])],"derivedFrom":subQ1}),1.0]])]});}
            var Q22;
            {var subQ0=sQuery(id+"F1.wireOp",EDGE,"E59.converted");var subQ1=sQuery(id+"F1.wireOp",EDGE,"E58.8.0");var subQ2=makeQuery(id+"F1.imprint","INTERSECT",VERTEX,{"derivedFrom":[subQ1,subQ0]});Q22=makeQuery(id+"F1.imprint","IMPRINT",FACE,{"disambiguationData":[TD([[makeQuery(id+"F1.imprint","IMPRINT",EDGE,{"disambiguationData":[TD([[subQ2,-1.0]])],"derivedFrom":subQ1}),1.0]])]});}
            var Q23;
            {var subQ0=sQuery(id+"F1.wireOp",EDGE,"E59.converted");var subQ1=sQuery(id+"F1.wireOp",EDGE,"E58.11.0");var subQ2=makeQuery(id+"F1.imprint","INTERSECT",VERTEX,{"derivedFrom":[subQ1,subQ0]});Q23=makeQuery(id+"F1.imprint","IMPRINT",FACE,{"disambiguationData":[TD([[makeQuery(id+"F1.imprint","IMPRINT",EDGE,{"disambiguationData":[TD([[subQ2,-1.0]])],"derivedFrom":subQ1}),-1.0]])]});}
            var Q24;
            {var subQ0=sQuery(id+"F1.wireOp",EDGE,"E59.converted");var subQ1=sQuery(id+"F1.wireOp",EDGE,"E58.5.0");var subQ2=makeQuery(id+"F1.imprint","INTERSECT",VERTEX,{"derivedFrom":[subQ1,subQ0]});Q24=makeQuery(id+"F1.imprint","IMPRINT",FACE,{"disambiguationData":[TD([[makeQuery(id+"F1.imprint","IMPRINT",EDGE,{"disambiguationData":[TD([[subQ2,-1.0]])],"derivedFrom":subQ1}),1.0]])]});}
            var Q25;
            {var subQ0=sQuery(id+"F1.wireOp",EDGE,"E59.converted");var subQ1=sQuery(id+"F1.wireOp",EDGE,"E58.5.1");var subQ2=makeQuery(id+"F1.imprint","INTERSECT",VERTEX,{"derivedFrom":[subQ1,subQ0]});Q25=makeQuery(id+"F1.imprint","IMPRINT",FACE,{"disambiguationData":[TD([[makeQuery(id+"F1.imprint","IMPRINT",EDGE,{"disambiguationData":[TD([[subQ2,-1.0]])],"derivedFrom":subQ1}),1.0]])]});}
            var Q26;
            {var subQ0=sQuery(id+"F1.wireOp",EDGE,"E59.converted");var subQ1=sQuery(id+"F1.wireOp",EDGE,"E58.11.0");var subQ2=makeQuery(id+"F1.imprint","INTERSECT",VERTEX,{"derivedFrom":[subQ1,subQ0]});Q26=makeQuery(id+"F1.imprint","IMPRINT",FACE,{"disambiguationData":[TD([[makeQuery(id+"F1.imprint","IMPRINT",EDGE,{"disambiguationData":[TD([[subQ2,-1.0]])],"derivedFrom":subQ1}),1.0]])]});}
            var Q27;
            {var subQ0=sQuery(id+"F1.wireOp",EDGE,"E64");var subQ1=sQuery(id+"F1.wireOp",EDGE,"E58.8.0");var subQ2=makeQuery(id+"F1.imprint","INTERSECT",VERTEX,{"derivedFrom":[subQ1,subQ0]});Q27=makeQuery(id+"F1.imprint","IMPRINT",FACE,{"disambiguationData":[TD([[makeQuery(id+"F1.imprint","IMPRINT",EDGE,{"disambiguationData":[TD([[subQ2,-1.0]])],"derivedFrom":subQ1}),1.0]])]});}
            var Q28;
            {var subQ0=sQuery(id+"F1.wireOp",EDGE,"E59.converted");var subQ1=sQuery(id+"F1.wireOp",EDGE,"E58.8.0");var subQ2=makeQuery(id+"F1.imprint","INTERSECT",VERTEX,{"derivedFrom":[subQ1,subQ0]});Q28=makeQuery(id+"F1.imprint","IMPRINT",FACE,{"disambiguationData":[TD([[makeQuery(id+"F1.imprint","IMPRINT",EDGE,{"disambiguationData":[TD([[subQ2,-1.0]])],"derivedFrom":subQ1}),-1.0]])]});}
            var Q29;
            {var subQ0=sQuery(id+"F1.wireOp",EDGE,"E64");var subQ1=sQuery(id+"F1.wireOp",EDGE,"E58.4.2");var subQ2=makeQuery(id+"F1.imprint","INTERSECT",VERTEX,{"derivedFrom":[subQ1,subQ0]});Q29=makeQuery(id+"F1.imprint","IMPRINT",FACE,{"disambiguationData":[TD([[makeQuery(id+"F1.imprint","IMPRINT",EDGE,{"disambiguationData":[TD([[subQ2,-1.0]])],"derivedFrom":subQ1}),-1.0]])]});}
            var Q30;
            {var subQ0=sQuery(id+"F1.wireOp",EDGE,"E59.converted");var subQ1=sQuery(id+"F1.wireOp",EDGE,"E58.12.0");var subQ2=makeQuery(id+"F1.imprint","INTERSECT",VERTEX,{"derivedFrom":[subQ1,subQ0]});Q30=makeQuery(id+"F1.imprint","IMPRINT",FACE,{"disambiguationData":[TD([[makeQuery(id+"F1.imprint","IMPRINT",EDGE,{"disambiguationData":[TD([[subQ2,-1.0]])],"derivedFrom":subQ1}),1.0]])]});}
            var Q31;
            {var subQ0=sQuery(id+"F1.wireOp",EDGE,"E64");var subQ1=sQuery(id+"F1.wireOp",EDGE,"E58.5.0");var subQ2=makeQuery(id+"F1.imprint","INTERSECT",VERTEX,{"derivedFrom":[subQ1,subQ0]});Q31=makeQuery(id+"F1.imprint","IMPRINT",FACE,{"disambiguationData":[TD([[makeQuery(id+"F1.imprint","IMPRINT",EDGE,{"disambiguationData":[TD([[subQ2,-1.0]])],"derivedFrom":subQ1}),1.0]])]});}
            var Q32;
            {var subQ0=sQuery(id+"F1.wireOp",EDGE,"E64");var subQ1=sQuery(id+"F1.wireOp",EDGE,"E58.10.0");var subQ2=makeQuery(id+"F1.imprint","INTERSECT",VERTEX,{"derivedFrom":[subQ1,subQ0]});Q32=makeQuery(id+"F1.imprint","IMPRINT",FACE,{"disambiguationData":[TD([[makeQuery(id+"F1.imprint","IMPRINT",EDGE,{"disambiguationData":[TD([[subQ2,-1.0]])],"derivedFrom":subQ1}),1.0]])]});}
            var Q33;
            {var subQ0=sQuery(id+"F1.wireOp",EDGE,"E64");var subQ1=sQuery(id+"F1.wireOp",EDGE,"E58.4.0");var subQ2=makeQuery(id+"F1.imprint","INTERSECT",VERTEX,{"derivedFrom":[subQ1,subQ0]});Q33=makeQuery(id+"F1.imprint","IMPRINT",FACE,{"disambiguationData":[TD([[makeQuery(id+"F1.imprint","IMPRINT",EDGE,{"disambiguationData":[TD([[subQ2,-1.0]])],"derivedFrom":subQ1}),-1.0]])]});}
            var Q34;
            {var subQ0=sQuery(id+"F1.wireOp",EDGE,"E64");var subQ1=sQuery(id+"F1.wireOp",EDGE,"E58.7.0");var subQ2=makeQuery(id+"F1.imprint","INTERSECT",VERTEX,{"derivedFrom":[subQ1,subQ0]});Q34=makeQuery(id+"F1.imprint","IMPRINT",FACE,{"disambiguationData":[TD([[makeQuery(id+"F1.imprint","IMPRINT",EDGE,{"disambiguationData":[TD([[subQ2,-1.0]])],"derivedFrom":subQ1}),1.0]])]});}
            var Q35;
            {var subQ0=sQuery(id+"F1.wireOp",EDGE,"E59.converted");var subQ1=sQuery(id+"F1.wireOp",EDGE,"E58.11.1");var subQ2=makeQuery(id+"F1.imprint","INTERSECT",VERTEX,{"derivedFrom":[subQ1,subQ0]});Q35=makeQuery(id+"F1.imprint","IMPRINT",FACE,{"disambiguationData":[TD([[makeQuery(id+"F1.imprint","IMPRINT",EDGE,{"disambiguationData":[TD([[subQ2,-1.0]])],"derivedFrom":subQ1}),1.0]])]});}
            var Q36;
            {var subQ0=sQuery(id+"F1.wireOp",EDGE,"E64");var subQ1=sQuery(id+"F1.wireOp",EDGE,"E58.11.0");var subQ2=makeQuery(id+"F1.imprint","INTERSECT",VERTEX,{"derivedFrom":[subQ1,subQ0]});Q36=makeQuery(id+"F1.imprint","IMPRINT",FACE,{"disambiguationData":[TD([[makeQuery(id+"F1.imprint","IMPRINT",EDGE,{"disambiguationData":[TD([[subQ2,-1.0]])],"derivedFrom":subQ1}),-1.0]])]});}
            var Q37;
            {var subQ0=sQuery(id+"F1.wireOp",EDGE,"E64");var subQ1=sQuery(id+"F1.wireOp",EDGE,"E58.6.0");var subQ2=makeQuery(id+"F1.imprint","INTERSECT",VERTEX,{"derivedFrom":[subQ1,subQ0]});Q37=makeQuery(id+"F1.imprint","IMPRINT",FACE,{"disambiguationData":[TD([[makeQuery(id+"F1.imprint","IMPRINT",EDGE,{"disambiguationData":[TD([[subQ2,-1.0]])],"derivedFrom":subQ1}),-1.0]])]});}
            var Q38;
            {var subQ0=sQuery(id+"F1.wireOp",EDGE,"E59.converted");var subQ1=sQuery(id+"F1.wireOp",EDGE,"E58.4.0");var subQ2=makeQuery(id+"F1.imprint","INTERSECT",VERTEX,{"derivedFrom":[subQ1,subQ0]});Q38=makeQuery(id+"F1.imprint","IMPRINT",FACE,{"disambiguationData":[TD([[makeQuery(id+"F1.imprint","IMPRINT",EDGE,{"disambiguationData":[TD([[subQ2,-1.0]])],"derivedFrom":subQ1}),1.0]])]});}
            var Q39;
            {var subQ0=sQuery(id+"F1.wireOp",EDGE,"E59.converted");var subQ1=sQuery(id+"F1.wireOp",EDGE,"E58.9.0");var subQ2=makeQuery(id+"F1.imprint","INTERSECT",VERTEX,{"derivedFrom":[subQ1,subQ0]});Q39=makeQuery(id+"F1.imprint","IMPRINT",FACE,{"disambiguationData":[TD([[makeQuery(id+"F1.imprint","IMPRINT",EDGE,{"disambiguationData":[TD([[subQ2,-1.0]])],"derivedFrom":subQ1}),1.0]])]});}
            var Q40;
            {var subQ0=sQuery(id+"F1.wireOp",EDGE,"E59.converted");var subQ1=sQuery(id+"F1.wireOp",EDGE,"E58.4.0");var subQ2=makeQuery(id+"F1.imprint","INTERSECT",VERTEX,{"derivedFrom":[subQ1,subQ0]});Q40=makeQuery(id+"F1.imprint","IMPRINT",FACE,{"disambiguationData":[TD([[makeQuery(id+"F1.imprint","IMPRINT",EDGE,{"disambiguationData":[TD([[subQ2,-1.0]])],"derivedFrom":subQ1}),-1.0]])]});}
            var Q41;
            {var subQ0=sQuery(id+"F1.wireOp",EDGE,"E59.converted");var subQ1=sQuery(id+"F1.wireOp",EDGE,"E58.5.0");var subQ2=makeQuery(id+"F1.imprint","INTERSECT",VERTEX,{"derivedFrom":[subQ1,subQ0]});Q41=makeQuery(id+"F1.imprint","IMPRINT",FACE,{"disambiguationData":[TD([[makeQuery(id+"F1.imprint","IMPRINT",EDGE,{"disambiguationData":[TD([[subQ2,-1.0]])],"derivedFrom":subQ1}),-1.0]])]});}
            var Q42;
            {var subQ0=sQuery(id+"F1.wireOp",EDGE,"E64");var subQ1=sQuery(id+"F1.wireOp",EDGE,"E58.8.0");var subQ2=makeQuery(id+"F1.imprint","INTERSECT",VERTEX,{"derivedFrom":[subQ1,subQ0]});Q42=makeQuery(id+"F1.imprint","IMPRINT",FACE,{"disambiguationData":[TD([[makeQuery(id+"F1.imprint","IMPRINT",EDGE,{"disambiguationData":[TD([[subQ2,-1.0]])],"derivedFrom":subQ1}),-1.0]])]});}
            var Q43;
            {var subQ0=sQuery(id+"F1.wireOp",EDGE,"E59.converted");var subQ1=sQuery(id+"F1.wireOp",EDGE,"E58.12.0");var subQ2=makeQuery(id+"F1.imprint","INTERSECT",VERTEX,{"derivedFrom":[subQ1,subQ0]});Q43=makeQuery(id+"F1.imprint","IMPRINT",FACE,{"disambiguationData":[TD([[makeQuery(id+"F1.imprint","IMPRINT",EDGE,{"disambiguationData":[TD([[subQ2,-1.0]])],"derivedFrom":subQ1}),-1.0]])]});}
            var Q44;
            {var subQ0=sQuery(id+"F1.wireOp",EDGE,"E64");var subQ1=sQuery(id+"F1.wireOp",EDGE,"E58.6.0");var subQ2=makeQuery(id+"F1.imprint","INTERSECT",VERTEX,{"derivedFrom":[subQ1,subQ0]});Q44=makeQuery(id+"F1.imprint","IMPRINT",FACE,{"disambiguationData":[TD([[makeQuery(id+"F1.imprint","IMPRINT",EDGE,{"disambiguationData":[TD([[subQ2,-1.0]])],"derivedFrom":subQ1}),1.0]])]});}
            var Q45;
            {var subQ0=sQuery(id+"F1.wireOp",EDGE,"E64");var subQ1=sQuery(id+"F1.wireOp",EDGE,"E58.4.0");var subQ2=makeQuery(id+"F1.imprint","INTERSECT",VERTEX,{"derivedFrom":[subQ1,subQ0]});Q45=makeQuery(id+"F1.imprint","IMPRINT",FACE,{"disambiguationData":[TD([[makeQuery(id+"F1.imprint","IMPRINT",EDGE,{"disambiguationData":[TD([[subQ2,-1.0]])],"derivedFrom":subQ1}),1.0]])]});}
            var Q46;
            {var subQ0=sQuery(id+"F1.wireOp",EDGE,"E64");var subQ1=sQuery(id+"F1.wireOp",EDGE,"E58.7.1");var subQ2=makeQuery(id+"F1.imprint","INTERSECT",VERTEX,{"derivedFrom":[subQ1,subQ0]});Q46=makeQuery(id+"F1.imprint","IMPRINT",FACE,{"disambiguationData":[TD([[makeQuery(id+"F1.imprint","IMPRINT",EDGE,{"disambiguationData":[TD([[subQ2,-1.0]])],"derivedFrom":subQ1}),1.0]])]});}
            var Q47;
            {var subQ0=sQuery(id+"F1.wireOp",EDGE,"E64");var subQ1=sQuery(id+"F1.wireOp",EDGE,"E58.6.1");var subQ2=makeQuery(id+"F1.imprint","INTERSECT",VERTEX,{"derivedFrom":[subQ1,subQ0]});Q47=makeQuery(id+"F1.imprint","IMPRINT",FACE,{"disambiguationData":[TD([[makeQuery(id+"F1.imprint","IMPRINT",EDGE,{"disambiguationData":[TD([[subQ2,-1.0]])],"derivedFrom":subQ1}),1.0]])]});}
            var Q48;
            {var subQ0=sQuery(id+"F1.wireOp",EDGE,"E59.converted");var subQ1=sQuery(id+"F1.wireOp",EDGE,"E58.6.1");var subQ2=makeQuery(id+"F1.imprint","INTERSECT",VERTEX,{"derivedFrom":[subQ1,subQ0]});Q48=makeQuery(id+"F1.imprint","IMPRINT",FACE,{"disambiguationData":[TD([[makeQuery(id+"F1.imprint","IMPRINT",EDGE,{"disambiguationData":[TD([[subQ2,-1.0]])],"derivedFrom":subQ1}),1.0]])]});}
            var Q49;
            {var subQ0=sQuery(id+"F1.wireOp",EDGE,"E64");var subQ1=sQuery(id+"F1.wireOp",EDGE,"E58.5.1");var subQ2=makeQuery(id+"F1.imprint","INTERSECT",VERTEX,{"derivedFrom":[subQ1,subQ0]});Q49=makeQuery(id+"F1.imprint","IMPRINT",FACE,{"disambiguationData":[TD([[makeQuery(id+"F1.imprint","IMPRINT",EDGE,{"disambiguationData":[TD([[subQ2,-1.0]])],"derivedFrom":subQ1}),1.0]])]});}
            var Q50;
            {var subQ0=sQuery(id+"F1.wireOp",EDGE,"E64");var subQ1=sQuery(id+"F1.wireOp",EDGE,"E58.8.1");var subQ2=makeQuery(id+"F1.imprint","INTERSECT",VERTEX,{"derivedFrom":[subQ1,subQ0]});Q50=makeQuery(id+"F1.imprint","IMPRINT",FACE,{"disambiguationData":[TD([[makeQuery(id+"F1.imprint","IMPRINT",EDGE,{"disambiguationData":[TD([[subQ2,-1.0]])],"derivedFrom":subQ1}),1.0]])]});}
            var Q51;
            {var subQ0=sQuery(id+"F1.wireOp",EDGE,"E59.converted");var subQ1=sQuery(id+"F1.wireOp",EDGE,"E58.10.0");var subQ2=makeQuery(id+"F1.imprint","INTERSECT",VERTEX,{"derivedFrom":[subQ1,subQ0]});Q51=makeQuery(id+"F1.imprint","IMPRINT",FACE,{"disambiguationData":[TD([[makeQuery(id+"F1.imprint","IMPRINT",EDGE,{"disambiguationData":[TD([[subQ2,-1.0]])],"derivedFrom":subQ1}),1.0]])]});}
            var Q52;
            {var subQ0=sQuery(id+"F1.wireOp",EDGE,"E64");var subQ1=sQuery(id+"F1.wireOp",EDGE,"E58.7.0");var subQ2=makeQuery(id+"F1.imprint","INTERSECT",VERTEX,{"derivedFrom":[subQ1,subQ0]});Q52=makeQuery(id+"F1.imprint","IMPRINT",FACE,{"disambiguationData":[TD([[makeQuery(id+"F1.imprint","IMPRINT",EDGE,{"disambiguationData":[TD([[subQ2,-1.0]])],"derivedFrom":subQ1}),-1.0]])]});}
            var Q53;
            {var subQ0=sQuery(id+"F1.wireOp",EDGE,"E64");var subQ1=sQuery(id+"F1.wireOp",EDGE,"E58.9.1");var subQ2=makeQuery(id+"F1.imprint","INTERSECT",VERTEX,{"derivedFrom":[subQ1,subQ0]});Q53=makeQuery(id+"F1.imprint","IMPRINT",FACE,{"disambiguationData":[TD([[makeQuery(id+"F1.imprint","IMPRINT",EDGE,{"disambiguationData":[TD([[subQ2,-1.0]])],"derivedFrom":subQ1}),1.0]])]});}
            var Q54;
            {var subQ0=sQuery(id+"F1.wireOp",EDGE,"E59.converted");var subQ1=sQuery(id+"F1.wireOp",EDGE,"E58.9.1");var subQ2=makeQuery(id+"F1.imprint","INTERSECT",VERTEX,{"derivedFrom":[subQ1,subQ0]});Q54=makeQuery(id+"F1.imprint","IMPRINT",FACE,{"disambiguationData":[TD([[makeQuery(id+"F1.imprint","IMPRINT",EDGE,{"disambiguationData":[TD([[subQ2,-1.0]])],"derivedFrom":subQ1}),1.0]])]});}
            extrude(context, id + "F11", {"entities" : qUnion([Q0, Q1, Q2, Q3, Q4, Q5, Q6, Q7, Q8, Q9, Q10, Q11, Q12, Q13, Q14, Q15, Q16, Q17, Q18, Q19, Q20, Q21, Q22, Q23, Q24, Q25, Q26, Q27, Q28, Q29, Q30, Q31, Q32, Q33, Q34, Q35, Q36, Q37, Q38, Q39, Q40, Q41, Q42, Q43, Q44, Q45, Q46, Q47, Q48, Q49, Q50, Q51, Q52, Q53, Q54]), "operationType" : NewBodyOperationType.ADD, "oppositeDirection" : true, "depth" : 1095.38 * mm, "offsetDistance" : 25.4 * mm, "hasSecondDirection" : true, "secondDirectionOppositeDirection" : true, "secondDirectionDepth" : 1092.2 * mm});
        }
        {
            var Q0;
            {var subQ0=sQuery(id+"F1.wireOp",EDGE,"E58.4.2");var subQ1=sQuery(id+"F1.wireOp",EDGE,"E57");var subQ2=makeQuery(id+"F1.imprint","INTERSECT",VERTEX,{"derivedFrom":[subQ1,subQ0]});Q0=makeQuery(id+"F1.imprint","IMPRINT",FACE,{"disambiguationData":[TD([[makeQuery(id+"F1.imprint","IMPRINT",EDGE,{"disambiguationData":[TD([[subQ2,1.0]])],"derivedFrom":subQ1}),1.0]])]});}
            var Q1;
            {var subQ0=sQuery(id+"F1.wireOp",EDGE,"E58.9.0");var subQ1=sQuery(id+"F1.wireOp",EDGE,"E57");var subQ2=makeQuery(id+"F1.imprint","INTERSECT",VERTEX,{"derivedFrom":[subQ1,subQ0]});Q1=makeQuery(id+"F1.imprint","IMPRINT",FACE,{"disambiguationData":[TD([[makeQuery(id+"F1.imprint","IMPRINT",EDGE,{"disambiguationData":[TD([[subQ2,-1.0]])],"derivedFrom":subQ1}),1.0]])]});}
            var Q2;
            {var subQ0=sQuery(id+"F1.wireOp",EDGE,"E58.11.0");var subQ1=sQuery(id+"F1.wireOp",EDGE,"E57");var subQ2=makeQuery(id+"F1.imprint","INTERSECT",VERTEX,{"derivedFrom":[subQ1,subQ0]});Q2=makeQuery(id+"F1.imprint","IMPRINT",FACE,{"disambiguationData":[TD([[makeQuery(id+"F1.imprint","IMPRINT",EDGE,{"disambiguationData":[TD([[subQ2,1.0]])],"derivedFrom":subQ1}),1.0]])]});}
            var Q3;
            {var subQ0=sQuery(id+"F1.wireOp",EDGE,"E58.12.1");var subQ1=sQuery(id+"F1.wireOp",EDGE,"E57");var subQ2=makeQuery(id+"F1.imprint","INTERSECT",VERTEX,{"derivedFrom":[subQ1,subQ0]});Q3=makeQuery(id+"F1.imprint","IMPRINT",FACE,{"disambiguationData":[TD([[makeQuery(id+"F1.imprint","IMPRINT",EDGE,{"disambiguationData":[TD([[subQ2,1.0]])],"derivedFrom":subQ1}),1.0]])]});}
            var Q4;
            {var subQ0=sQuery(id+"F1.wireOp",EDGE,"E58.10.0");var subQ1=sQuery(id+"F1.wireOp",EDGE,"E57");var subQ2=makeQuery(id+"F1.imprint","INTERSECT",VERTEX,{"derivedFrom":[subQ1,subQ0]});Q4=makeQuery(id+"F1.imprint","IMPRINT",FACE,{"disambiguationData":[TD([[makeQuery(id+"F1.imprint","IMPRINT",EDGE,{"disambiguationData":[TD([[subQ2,-1.0]])],"derivedFrom":subQ1}),1.0]])]});}
            var Q5;
            {var subQ0=sQuery(id+"F1.wireOp",EDGE,"E58.4.2");var subQ1=sQuery(id+"F1.wireOp",EDGE,"E57");var subQ2=makeQuery(id+"F1.imprint","INTERSECT",VERTEX,{"derivedFrom":[subQ1,subQ0]});Q5=makeQuery(id+"F1.imprint","IMPRINT",FACE,{"disambiguationData":[TD([[makeQuery(id+"F1.imprint","IMPRINT",EDGE,{"disambiguationData":[TD([[subQ2,-1.0]])],"derivedFrom":subQ1}),1.0]])]});}
            var Q6;
            {var subQ0=sQuery(id+"F1.wireOp",EDGE,"E58.7.1");var subQ1=sQuery(id+"F1.wireOp",EDGE,"E57");var subQ2=makeQuery(id+"F1.imprint","INTERSECT",VERTEX,{"derivedFrom":[subQ1,subQ0]});Q6=makeQuery(id+"F1.imprint","IMPRINT",FACE,{"disambiguationData":[TD([[makeQuery(id+"F1.imprint","IMPRINT",EDGE,{"disambiguationData":[TD([[subQ2,-1.0]])],"derivedFrom":subQ1}),1.0]])]});}
            var Q7;
            {var subQ0=sQuery(id+"F1.wireOp",EDGE,"E58.4.1");var subQ1=sQuery(id+"F1.wireOp",EDGE,"E57");var subQ2=makeQuery(id+"F1.imprint","INTERSECT",VERTEX,{"derivedFrom":[subQ1,subQ0]});Q7=makeQuery(id+"F1.imprint","IMPRINT",FACE,{"disambiguationData":[TD([[makeQuery(id+"F1.imprint","IMPRINT",EDGE,{"disambiguationData":[TD([[subQ2,1.0]])],"derivedFrom":subQ1}),1.0]])]});}
            var Q8;
            {var subQ0=sQuery(id+"F1.wireOp",EDGE,"E58.9.1");var subQ1=sQuery(id+"F1.wireOp",EDGE,"E57");var subQ2=makeQuery(id+"F1.imprint","INTERSECT",VERTEX,{"derivedFrom":[subQ1,subQ0]});Q8=makeQuery(id+"F1.imprint","IMPRINT",FACE,{"disambiguationData":[TD([[makeQuery(id+"F1.imprint","IMPRINT",EDGE,{"disambiguationData":[TD([[subQ2,-1.0]])],"derivedFrom":subQ1}),1.0]])]});}
            var Q9;
            {var subQ0=sQuery(id+"F1.wireOp",EDGE,"E58.5.0");var subQ1=sQuery(id+"F1.wireOp",EDGE,"E57");var subQ2=makeQuery(id+"F1.imprint","INTERSECT",VERTEX,{"derivedFrom":[subQ1,subQ0]});Q9=makeQuery(id+"F1.imprint","IMPRINT",FACE,{"disambiguationData":[TD([[makeQuery(id+"F1.imprint","IMPRINT",EDGE,{"disambiguationData":[TD([[subQ2,1.0]])],"derivedFrom":subQ1}),1.0]])]});}
            var Q10;
            {var subQ0=sQuery(id+"F1.wireOp",EDGE,"E58.8.0");var subQ1=sQuery(id+"F1.wireOp",EDGE,"E57");var subQ2=makeQuery(id+"F1.imprint","INTERSECT",VERTEX,{"derivedFrom":[subQ1,subQ0]});Q10=makeQuery(id+"F1.imprint","IMPRINT",FACE,{"disambiguationData":[TD([[makeQuery(id+"F1.imprint","IMPRINT",EDGE,{"disambiguationData":[TD([[subQ2,-1.0]])],"derivedFrom":subQ1}),1.0]])]});}
            var Q11;
            {var subQ0=sQuery(id+"F1.wireOp",EDGE,"E58.8.1");var subQ1=sQuery(id+"F1.wireOp",EDGE,"E57");var subQ2=makeQuery(id+"F1.imprint","INTERSECT",VERTEX,{"derivedFrom":[subQ1,subQ0]});Q11=makeQuery(id+"F1.imprint","IMPRINT",FACE,{"disambiguationData":[TD([[makeQuery(id+"F1.imprint","IMPRINT",EDGE,{"disambiguationData":[TD([[subQ2,-1.0]])],"derivedFrom":subQ1}),1.0]])]});}
            var Q12;
            {var subQ5=sQuery(id+"F1.wireOp",EDGE,"E58.4.0");var subQ7=sQuery(id+"F1.wireOp",EDGE,"E55");var subQ8=makeQuery(id+"F1.imprint","INTERSECT",VERTEX,{"derivedFrom":[subQ7,subQ5]});Q12=makeQuery(id+"F1.imprint","IMPRINT",FACE,{"disambiguationData":[TD([[makeQuery(id+"F1.imprint","IMPRINT",EDGE,{"disambiguationData":[TD([[subQ8,1.0]])],"derivedFrom":subQ7}),1.0]])]});}
            var Q13;
            {var subQ0=sQuery(id+"F1.wireOp",EDGE,"E58.10.1");var subQ1=sQuery(id+"F1.wireOp",EDGE,"E57");var subQ2=makeQuery(id+"F1.imprint","INTERSECT",VERTEX,{"derivedFrom":[subQ1,subQ0]});Q13=makeQuery(id+"F1.imprint","IMPRINT",FACE,{"disambiguationData":[TD([[makeQuery(id+"F1.imprint","IMPRINT",EDGE,{"disambiguationData":[TD([[subQ2,-1.0]])],"derivedFrom":subQ1}),1.0]])]});}
            var Q14;
            {var subQ0=sQuery(id+"F1.wireOp",EDGE,"E58.9.0");var subQ1=sQuery(id+"F1.wireOp",EDGE,"E57");var subQ2=makeQuery(id+"F1.imprint","INTERSECT",VERTEX,{"derivedFrom":[subQ1,subQ0]});Q14=makeQuery(id+"F1.imprint","IMPRINT",FACE,{"disambiguationData":[TD([[makeQuery(id+"F1.imprint","IMPRINT",EDGE,{"disambiguationData":[TD([[subQ2,1.0]])],"derivedFrom":subQ1}),1.0]])]});}
            var Q15;
            {var subQ0=sQuery(id+"F1.wireOp",EDGE,"E58.5.0");var subQ1=sQuery(id+"F1.wireOp",EDGE,"E57");var subQ2=makeQuery(id+"F1.imprint","INTERSECT",VERTEX,{"derivedFrom":[subQ1,subQ0]});Q15=makeQuery(id+"F1.imprint","IMPRINT",FACE,{"disambiguationData":[TD([[makeQuery(id+"F1.imprint","IMPRINT",EDGE,{"disambiguationData":[TD([[subQ2,-1.0]])],"derivedFrom":subQ1}),1.0]])]});}
            var Q16;
            {var subQ17=sQuery(id+"F1.wireOp",EDGE,"E58.4.0");var subQ19=sQuery(id+"F1.wireOp",EDGE,"E55");var subQ20=makeQuery(id+"F1.imprint","INTERSECT",VERTEX,{"derivedFrom":[subQ19,subQ17]});Q16=makeQuery(id+"F1.imprint","IMPRINT",FACE,{"disambiguationData":[TD([[makeQuery(id+"F1.imprint","IMPRINT",EDGE,{"disambiguationData":[TD([[subQ20,-1.0]])],"derivedFrom":subQ19}),1.0]])]});}
            var Q17;
            {var subQ0=sQuery(id+"F1.wireOp",EDGE,"E58.7.0");var subQ1=sQuery(id+"F1.wireOp",EDGE,"E57");var subQ2=makeQuery(id+"F1.imprint","INTERSECT",VERTEX,{"derivedFrom":[subQ1,subQ0]});Q17=makeQuery(id+"F1.imprint","IMPRINT",FACE,{"disambiguationData":[TD([[makeQuery(id+"F1.imprint","IMPRINT",EDGE,{"disambiguationData":[TD([[subQ2,-1.0]])],"derivedFrom":subQ1}),1.0]])]});}
            var Q18;
            {var subQ0=sQuery(id+"F1.wireOp",EDGE,"E58.5.1");var subQ1=sQuery(id+"F1.wireOp",EDGE,"E57");var subQ2=makeQuery(id+"F1.imprint","INTERSECT",VERTEX,{"derivedFrom":[subQ1,subQ0]});Q18=makeQuery(id+"F1.imprint","IMPRINT",FACE,{"disambiguationData":[TD([[makeQuery(id+"F1.imprint","IMPRINT",EDGE,{"disambiguationData":[TD([[subQ2,-1.0]])],"derivedFrom":subQ1}),1.0]])]});}
            var Q19;
            {var subQ0=sQuery(id+"F1.wireOp",EDGE,"E58.7.0");var subQ1=sQuery(id+"F1.wireOp",EDGE,"E57");var subQ2=makeQuery(id+"F1.imprint","INTERSECT",VERTEX,{"derivedFrom":[subQ1,subQ0]});Q19=makeQuery(id+"F1.imprint","IMPRINT",FACE,{"disambiguationData":[TD([[makeQuery(id+"F1.imprint","IMPRINT",EDGE,{"disambiguationData":[TD([[subQ2,1.0]])],"derivedFrom":subQ1}),1.0]])]});}
            var Q20;
            {var subQ0=sQuery(id+"F1.wireOp",EDGE,"E58.12.2");var subQ1=sQuery(id+"F1.wireOp",EDGE,"E57");var subQ2=makeQuery(id+"F1.imprint","INTERSECT",VERTEX,{"derivedFrom":[subQ1,subQ0]});Q20=makeQuery(id+"F1.imprint","IMPRINT",FACE,{"disambiguationData":[TD([[makeQuery(id+"F1.imprint","IMPRINT",EDGE,{"disambiguationData":[TD([[subQ2,-1.0]])],"derivedFrom":subQ1}),1.0]])]});}
            var Q21;
            {var subQ0=sQuery(id+"F1.wireOp",EDGE,"E58.4.1");var subQ1=sQuery(id+"F1.wireOp",EDGE,"E57");var subQ2=makeQuery(id+"F1.imprint","INTERSECT",VERTEX,{"derivedFrom":[subQ1,subQ0]});Q21=makeQuery(id+"F1.imprint","IMPRINT",FACE,{"disambiguationData":[TD([[makeQuery(id+"F1.imprint","IMPRINT",EDGE,{"disambiguationData":[TD([[subQ2,-1.0]])],"derivedFrom":subQ1}),1.0]])]});}
            var Q22;
            {var subQ0=sQuery(id+"F1.wireOp",EDGE,"E58.8.0");var subQ1=sQuery(id+"F1.wireOp",EDGE,"E57");var subQ2=makeQuery(id+"F1.imprint","INTERSECT",VERTEX,{"derivedFrom":[subQ1,subQ0]});Q22=makeQuery(id+"F1.imprint","IMPRINT",FACE,{"disambiguationData":[TD([[makeQuery(id+"F1.imprint","IMPRINT",EDGE,{"disambiguationData":[TD([[subQ2,1.0]])],"derivedFrom":subQ1}),1.0]])]});}
            var Q23;
            {var subQ0=sQuery(id+"F1.wireOp",EDGE,"E58.6.0");var subQ1=sQuery(id+"F1.wireOp",EDGE,"E57");var subQ2=makeQuery(id+"F1.imprint","INTERSECT",VERTEX,{"derivedFrom":[subQ1,subQ0]});Q23=makeQuery(id+"F1.imprint","IMPRINT",FACE,{"disambiguationData":[TD([[makeQuery(id+"F1.imprint","IMPRINT",EDGE,{"disambiguationData":[TD([[subQ2,1.0]])],"derivedFrom":subQ1}),1.0]])]});}
            var Q24;
            {var subQ0=sQuery(id+"F1.wireOp",EDGE,"E58.10.0");var subQ1=sQuery(id+"F1.wireOp",EDGE,"E57");var subQ2=makeQuery(id+"F1.imprint","INTERSECT",VERTEX,{"derivedFrom":[subQ1,subQ0]});Q24=makeQuery(id+"F1.imprint","IMPRINT",FACE,{"disambiguationData":[TD([[makeQuery(id+"F1.imprint","IMPRINT",EDGE,{"disambiguationData":[TD([[subQ2,1.0]])],"derivedFrom":subQ1}),1.0]])]});}
            var Q25;
            {var subQ0=sQuery(id+"F1.wireOp",EDGE,"E58.6.1");var subQ1=sQuery(id+"F1.wireOp",EDGE,"E57");var subQ2=makeQuery(id+"F1.imprint","INTERSECT",VERTEX,{"derivedFrom":[subQ1,subQ0]});Q25=makeQuery(id+"F1.imprint","IMPRINT",FACE,{"disambiguationData":[TD([[makeQuery(id+"F1.imprint","IMPRINT",EDGE,{"disambiguationData":[TD([[subQ2,-1.0]])],"derivedFrom":subQ1}),1.0]])]});}
            var Q26;
            {var subQ0=sQuery(id+"F1.wireOp",EDGE,"E58.6.0");var subQ1=sQuery(id+"F1.wireOp",EDGE,"E57");var subQ2=makeQuery(id+"F1.imprint","INTERSECT",VERTEX,{"derivedFrom":[subQ1,subQ0]});Q26=makeQuery(id+"F1.imprint","IMPRINT",FACE,{"disambiguationData":[TD([[makeQuery(id+"F1.imprint","IMPRINT",EDGE,{"disambiguationData":[TD([[subQ2,-1.0]])],"derivedFrom":subQ1}),1.0]])]});}
            var Q27;
            {var subQ0=sQuery(id+"F1.wireOp",EDGE,"E58.11.0");var subQ1=sQuery(id+"F1.wireOp",EDGE,"E57");var subQ2=makeQuery(id+"F1.imprint","INTERSECT",VERTEX,{"derivedFrom":[subQ1,subQ0]});Q27=makeQuery(id+"F1.imprint","IMPRINT",FACE,{"disambiguationData":[TD([[makeQuery(id+"F1.imprint","IMPRINT",EDGE,{"disambiguationData":[TD([[subQ2,-1.0]])],"derivedFrom":subQ1}),1.0]])]});}
            var Q28;
            {var subQ0=sQuery(id+"F1.wireOp",EDGE,"E58.11.1");var subQ1=sQuery(id+"F1.wireOp",EDGE,"E57");var subQ2=makeQuery(id+"F1.imprint","INTERSECT",VERTEX,{"derivedFrom":[subQ1,subQ0]});Q28=makeQuery(id+"F1.imprint","IMPRINT",FACE,{"disambiguationData":[TD([[makeQuery(id+"F1.imprint","IMPRINT",EDGE,{"disambiguationData":[TD([[subQ2,-1.0]])],"derivedFrom":subQ1}),1.0]])]});}
            var Q29;
            {var subQ0=sQuery(id+"F1.wireOp",EDGE,"E63");var subQ1=sQuery(id+"F1.wireOp",EDGE,"E58.10.1");var subQ2=makeQuery(id+"F1.imprint","INTERSECT",VERTEX,{"derivedFrom":[subQ1,subQ0]});Q29=makeQuery(id+"F1.imprint","IMPRINT",FACE,{"disambiguationData":[TD([[makeQuery(id+"F1.imprint","IMPRINT",EDGE,{"disambiguationData":[TD([[subQ2,-1.0]])],"derivedFrom":subQ1}),1.0]])]});}
            var Q30;
            {var subQ0=sQuery(id+"F1.wireOp",EDGE,"E63");var subQ1=sQuery(id+"F1.wireOp",EDGE,"E58.9.1");var subQ2=makeQuery(id+"F1.imprint","INTERSECT",VERTEX,{"derivedFrom":[subQ1,subQ0]});Q30=makeQuery(id+"F1.imprint","IMPRINT",FACE,{"disambiguationData":[TD([[makeQuery(id+"F1.imprint","IMPRINT",EDGE,{"disambiguationData":[TD([[subQ2,-1.0]])],"derivedFrom":subQ1}),1.0]])]});}
            var Q31;
            {var subQ0=sQuery(id+"F1.wireOp",EDGE,"E63");var subQ1=sQuery(id+"F1.wireOp",EDGE,"E58.11.1");var subQ2=makeQuery(id+"F1.imprint","INTERSECT",VERTEX,{"derivedFrom":[subQ1,subQ0]});Q31=makeQuery(id+"F1.imprint","IMPRINT",FACE,{"disambiguationData":[TD([[makeQuery(id+"F1.imprint","IMPRINT",EDGE,{"disambiguationData":[TD([[subQ2,-1.0]])],"derivedFrom":subQ1}),1.0]])]});}
            var Q32;
            {var subQ0=sQuery(id+"F1.wireOp",EDGE,"E63");var subQ1=sQuery(id+"F1.wireOp",EDGE,"E58.4.2");var subQ2=makeQuery(id+"F1.imprint","INTERSECT",VERTEX,{"derivedFrom":[subQ1,subQ0]});Q32=makeQuery(id+"F1.imprint","IMPRINT",FACE,{"disambiguationData":[TD([[makeQuery(id+"F1.imprint","IMPRINT",EDGE,{"disambiguationData":[TD([[subQ2,-1.0]])],"derivedFrom":subQ1}),-1.0]])]});}
            var Q33;
            {var subQ0=sQuery(id+"F1.wireOp",EDGE,"E63");var subQ1=sQuery(id+"F1.wireOp",EDGE,"E58.4.1");var subQ2=makeQuery(id+"F1.imprint","INTERSECT",VERTEX,{"derivedFrom":[subQ1,subQ0]});Q33=makeQuery(id+"F1.imprint","IMPRINT",FACE,{"disambiguationData":[TD([[makeQuery(id+"F1.imprint","IMPRINT",EDGE,{"disambiguationData":[TD([[subQ2,-1.0]])],"derivedFrom":subQ1}),1.0]])]});}
            var Q34;
            {var subQ0=sQuery(id+"F1.wireOp",EDGE,"E63");var subQ1=sQuery(id+"F1.wireOp",EDGE,"E58.5.1");var subQ2=makeQuery(id+"F1.imprint","INTERSECT",VERTEX,{"derivedFrom":[subQ1,subQ0]});Q34=makeQuery(id+"F1.imprint","IMPRINT",FACE,{"disambiguationData":[TD([[makeQuery(id+"F1.imprint","IMPRINT",EDGE,{"disambiguationData":[TD([[subQ2,-1.0]])],"derivedFrom":subQ1}),1.0]])]});}
            var Q35;
            {var subQ0=sQuery(id+"F1.wireOp",EDGE,"E63");var subQ1=sQuery(id+"F1.wireOp",EDGE,"E58.6.1");var subQ2=makeQuery(id+"F1.imprint","INTERSECT",VERTEX,{"derivedFrom":[subQ1,subQ0]});Q35=makeQuery(id+"F1.imprint","IMPRINT",FACE,{"disambiguationData":[TD([[makeQuery(id+"F1.imprint","IMPRINT",EDGE,{"disambiguationData":[TD([[subQ2,-1.0]])],"derivedFrom":subQ1}),1.0]])]});}
            var Q36;
            {var subQ0=sQuery(id+"F1.wireOp",EDGE,"E63");var subQ1=sQuery(id+"F1.wireOp",EDGE,"E58.7.1");var subQ2=makeQuery(id+"F1.imprint","INTERSECT",VERTEX,{"derivedFrom":[subQ1,subQ0]});Q36=makeQuery(id+"F1.imprint","IMPRINT",FACE,{"disambiguationData":[TD([[makeQuery(id+"F1.imprint","IMPRINT",EDGE,{"disambiguationData":[TD([[subQ2,-1.0]])],"derivedFrom":subQ1}),1.0]])]});}
            var Q37;
            {var subQ0=sQuery(id+"F1.wireOp",EDGE,"E63");var subQ1=sQuery(id+"F1.wireOp",EDGE,"E58.8.1");var subQ2=makeQuery(id+"F1.imprint","INTERSECT",VERTEX,{"derivedFrom":[subQ1,subQ0]});Q37=makeQuery(id+"F1.imprint","IMPRINT",FACE,{"disambiguationData":[TD([[makeQuery(id+"F1.imprint","IMPRINT",EDGE,{"disambiguationData":[TD([[subQ2,-1.0]])],"derivedFrom":subQ1}),1.0]])]});}
            var Q38;
            {var subQ0=sQuery(id+"F1.wireOp",EDGE,"E63");var subQ1=sQuery(id+"F1.wireOp",EDGE,"E58.12.0");var subQ2=makeQuery(id+"F1.imprint","INTERSECT",VERTEX,{"derivedFrom":[subQ1,subQ0]});Q38=makeQuery(id+"F1.imprint","IMPRINT",FACE,{"disambiguationData":[TD([[makeQuery(id+"F1.imprint","IMPRINT",EDGE,{"disambiguationData":[TD([[subQ2,-1.0]])],"derivedFrom":subQ1}),1.0]])]});}
            var Q39;
            {var subQ0=sQuery(id+"F1.wireOp",EDGE,"E63");var subQ1=sQuery(id+"F1.wireOp",EDGE,"E58.12.0");var subQ2=makeQuery(id+"F1.imprint","INTERSECT",VERTEX,{"derivedFrom":[subQ1,subQ0]});Q39=makeQuery(id+"F1.imprint","IMPRINT",FACE,{"disambiguationData":[TD([[makeQuery(id+"F1.imprint","IMPRINT",EDGE,{"disambiguationData":[TD([[subQ2,-1.0]])],"derivedFrom":subQ1}),-1.0]])]});}
            var Q40;
            {var subQ0=sQuery(id+"F1.wireOp",EDGE,"E63");var subQ1=sQuery(id+"F1.wireOp",EDGE,"E58.11.0");var subQ2=makeQuery(id+"F1.imprint","INTERSECT",VERTEX,{"derivedFrom":[subQ1,subQ0]});Q40=makeQuery(id+"F1.imprint","IMPRINT",FACE,{"disambiguationData":[TD([[makeQuery(id+"F1.imprint","IMPRINT",EDGE,{"disambiguationData":[TD([[subQ2,-1.0]])],"derivedFrom":subQ1}),-1.0]])]});}
            var Q41;
            {var subQ0=sQuery(id+"F1.wireOp",EDGE,"E63");var subQ1=sQuery(id+"F1.wireOp",EDGE,"E58.11.0");var subQ2=makeQuery(id+"F1.imprint","INTERSECT",VERTEX,{"derivedFrom":[subQ1,subQ0]});Q41=makeQuery(id+"F1.imprint","IMPRINT",FACE,{"disambiguationData":[TD([[makeQuery(id+"F1.imprint","IMPRINT",EDGE,{"disambiguationData":[TD([[subQ2,-1.0]])],"derivedFrom":subQ1}),1.0]])]});}
            var Q42;
            {var subQ0=sQuery(id+"F1.wireOp",EDGE,"E63");var subQ1=sQuery(id+"F1.wireOp",EDGE,"E58.10.0");var subQ2=makeQuery(id+"F1.imprint","INTERSECT",VERTEX,{"derivedFrom":[subQ1,subQ0]});Q42=makeQuery(id+"F1.imprint","IMPRINT",FACE,{"disambiguationData":[TD([[makeQuery(id+"F1.imprint","IMPRINT",EDGE,{"disambiguationData":[TD([[subQ2,-1.0]])],"derivedFrom":subQ1}),-1.0]])]});}
            var Q43;
            {var subQ0=sQuery(id+"F1.wireOp",EDGE,"E63");var subQ1=sQuery(id+"F1.wireOp",EDGE,"E58.10.0");var subQ2=makeQuery(id+"F1.imprint","INTERSECT",VERTEX,{"derivedFrom":[subQ1,subQ0]});Q43=makeQuery(id+"F1.imprint","IMPRINT",FACE,{"disambiguationData":[TD([[makeQuery(id+"F1.imprint","IMPRINT",EDGE,{"disambiguationData":[TD([[subQ2,-1.0]])],"derivedFrom":subQ1}),1.0]])]});}
            var Q44;
            {var subQ0=sQuery(id+"F1.wireOp",EDGE,"E63");var subQ1=sQuery(id+"F1.wireOp",EDGE,"E58.8.0");var subQ2=makeQuery(id+"F1.imprint","INTERSECT",VERTEX,{"derivedFrom":[subQ1,subQ0]});Q44=makeQuery(id+"F1.imprint","IMPRINT",FACE,{"disambiguationData":[TD([[makeQuery(id+"F1.imprint","IMPRINT",EDGE,{"disambiguationData":[TD([[subQ2,-1.0]])],"derivedFrom":subQ1}),-1.0]])]});}
            var Q45;
            {var subQ0=sQuery(id+"F1.wireOp",EDGE,"E63");var subQ1=sQuery(id+"F1.wireOp",EDGE,"E58.7.0");var subQ2=makeQuery(id+"F1.imprint","INTERSECT",VERTEX,{"derivedFrom":[subQ1,subQ0]});Q45=makeQuery(id+"F1.imprint","IMPRINT",FACE,{"disambiguationData":[TD([[makeQuery(id+"F1.imprint","IMPRINT",EDGE,{"disambiguationData":[TD([[subQ2,-1.0]])],"derivedFrom":subQ1}),-1.0]])]});}
            var Q46;
            {var subQ0=sQuery(id+"F1.wireOp",EDGE,"E63");var subQ1=sQuery(id+"F1.wireOp",EDGE,"E58.7.0");var subQ2=makeQuery(id+"F1.imprint","INTERSECT",VERTEX,{"derivedFrom":[subQ1,subQ0]});Q46=makeQuery(id+"F1.imprint","IMPRINT",FACE,{"disambiguationData":[TD([[makeQuery(id+"F1.imprint","IMPRINT",EDGE,{"disambiguationData":[TD([[subQ2,-1.0]])],"derivedFrom":subQ1}),1.0]])]});}
            var Q47;
            {var subQ0=sQuery(id+"F1.wireOp",EDGE,"E63");var subQ1=sQuery(id+"F1.wireOp",EDGE,"E58.9.0");var subQ2=makeQuery(id+"F1.imprint","INTERSECT",VERTEX,{"derivedFrom":[subQ1,subQ0]});Q47=makeQuery(id+"F1.imprint","IMPRINT",FACE,{"disambiguationData":[TD([[makeQuery(id+"F1.imprint","IMPRINT",EDGE,{"disambiguationData":[TD([[subQ2,-1.0]])],"derivedFrom":subQ1}),-1.0]])]});}
            var Q48;
            {var subQ0=sQuery(id+"F1.wireOp",EDGE,"E63");var subQ1=sQuery(id+"F1.wireOp",EDGE,"E58.9.0");var subQ2=makeQuery(id+"F1.imprint","INTERSECT",VERTEX,{"derivedFrom":[subQ1,subQ0]});Q48=makeQuery(id+"F1.imprint","IMPRINT",FACE,{"disambiguationData":[TD([[makeQuery(id+"F1.imprint","IMPRINT",EDGE,{"disambiguationData":[TD([[subQ2,-1.0]])],"derivedFrom":subQ1}),1.0]])]});}
            var Q49;
            {var subQ0=sQuery(id+"F1.wireOp",EDGE,"E63");var subQ1=sQuery(id+"F1.wireOp",EDGE,"E58.6.0");var subQ2=makeQuery(id+"F1.imprint","INTERSECT",VERTEX,{"derivedFrom":[subQ1,subQ0]});Q49=makeQuery(id+"F1.imprint","IMPRINT",FACE,{"disambiguationData":[TD([[makeQuery(id+"F1.imprint","IMPRINT",EDGE,{"disambiguationData":[TD([[subQ2,-1.0]])],"derivedFrom":subQ1}),1.0]])]});}
            var Q50;
            {var subQ0=sQuery(id+"F1.wireOp",EDGE,"E63");var subQ1=sQuery(id+"F1.wireOp",EDGE,"E58.6.0");var subQ2=makeQuery(id+"F1.imprint","INTERSECT",VERTEX,{"derivedFrom":[subQ1,subQ0]});Q50=makeQuery(id+"F1.imprint","IMPRINT",FACE,{"disambiguationData":[TD([[makeQuery(id+"F1.imprint","IMPRINT",EDGE,{"disambiguationData":[TD([[subQ2,-1.0]])],"derivedFrom":subQ1}),-1.0]])]});}
            var Q51;
            {var subQ0=sQuery(id+"F1.wireOp",EDGE,"E63");var subQ1=sQuery(id+"F1.wireOp",EDGE,"E58.8.0");var subQ2=makeQuery(id+"F1.imprint","INTERSECT",VERTEX,{"derivedFrom":[subQ1,subQ0]});Q51=makeQuery(id+"F1.imprint","IMPRINT",FACE,{"disambiguationData":[TD([[makeQuery(id+"F1.imprint","IMPRINT",EDGE,{"disambiguationData":[TD([[subQ2,-1.0]])],"derivedFrom":subQ1}),1.0]])]});}
            var Q52;
            {var subQ0=sQuery(id+"F1.wireOp",EDGE,"E63");var subQ1=sQuery(id+"F1.wireOp",EDGE,"E58.5.0");var subQ2=makeQuery(id+"F1.imprint","INTERSECT",VERTEX,{"derivedFrom":[subQ1,subQ0]});Q52=makeQuery(id+"F1.imprint","IMPRINT",FACE,{"disambiguationData":[TD([[makeQuery(id+"F1.imprint","IMPRINT",EDGE,{"disambiguationData":[TD([[subQ2,-1.0]])],"derivedFrom":subQ1}),1.0]])]});}
            var Q53;
            {var subQ0=sQuery(id+"F1.wireOp",EDGE,"E63");var subQ1=sQuery(id+"F1.wireOp",EDGE,"E58.5.0");var subQ2=makeQuery(id+"F1.imprint","INTERSECT",VERTEX,{"derivedFrom":[subQ1,subQ0]});Q53=makeQuery(id+"F1.imprint","IMPRINT",FACE,{"disambiguationData":[TD([[makeQuery(id+"F1.imprint","IMPRINT",EDGE,{"disambiguationData":[TD([[subQ2,-1.0]])],"derivedFrom":subQ1}),-1.0]])]});}
            var Q54;
            {var subQ0=sQuery(id+"F1.wireOp",EDGE,"E63");var subQ1=sQuery(id+"F1.wireOp",EDGE,"E58.4.0");var subQ2=makeQuery(id+"F1.imprint","INTERSECT",VERTEX,{"derivedFrom":[subQ1,subQ0]});Q54=makeQuery(id+"F1.imprint","IMPRINT",FACE,{"disambiguationData":[TD([[makeQuery(id+"F1.imprint","IMPRINT",EDGE,{"disambiguationData":[TD([[subQ2,-1.0]])],"derivedFrom":subQ1}),1.0]])]});}
            var Q55;
            {var subQ0=sQuery(id+"F1.wireOp",EDGE,"E63");var subQ1=sQuery(id+"F1.wireOp",EDGE,"E58.4.0");var subQ2=makeQuery(id+"F1.imprint","INTERSECT",VERTEX,{"derivedFrom":[subQ1,subQ0]});Q55=makeQuery(id+"F1.imprint","IMPRINT",FACE,{"disambiguationData":[TD([[makeQuery(id+"F1.imprint","IMPRINT",EDGE,{"disambiguationData":[TD([[subQ2,-1.0]])],"derivedFrom":subQ1}),-1.0]])]});}
            extrude(context, id + "F12", {"entities" : qUnion([Q0, Q1, Q2, Q3, Q4, Q5, Q6, Q7, Q8, Q9, Q10, Q11, Q12, Q13, Q14, Q15, Q16, Q17, Q18, Q19, Q20, Q21, Q22, Q23, Q24, Q25, Q26, Q27, Q28, Q29, Q30, Q31, Q32, Q33, Q34, Q35, Q36, Q37, Q38, Q39, Q40, Q41, Q42, Q43, Q44, Q45, Q46, Q47, Q48, Q49, Q50, Q51, Q52, Q53, Q54, Q55]), "operationType" : NewBodyOperationType.ADD, "oppositeDirection" : true, "depth" : 1019.17 * mm, "offsetDistance" : 25.4 * mm, "hasSecondDirection" : true, "secondDirectionOppositeDirection" : true, "secondDirectionDepth" : 1016 * mm});
        }
        {
            var Q0;
            {var subQ0=sQuery(id+"F1.wireOp",EDGE,"E64");var subQ1=sQuery(id+"F1.wireOp",EDGE,"E58.11.1");var subQ2=makeQuery(id+"F1.imprint","INTERSECT",VERTEX,{"derivedFrom":[subQ1,subQ0]});Q0=makeQuery(id+"F1.imprint","IMPRINT",FACE,{"disambiguationData":[TD([[makeQuery(id+"F1.imprint","IMPRINT",EDGE,{"disambiguationData":[TD([[subQ2,-1.0]])],"derivedFrom":subQ1}),1.0]])]});}
            var Q1;
            {var subQ0=sQuery(id+"F1.wireOp",EDGE,"E64");var subQ1=sQuery(id+"F1.wireOp",EDGE,"E58.6.0");var subQ2=makeQuery(id+"F1.imprint","INTERSECT",VERTEX,{"derivedFrom":[subQ1,subQ0]});Q1=makeQuery(id+"F1.imprint","IMPRINT",FACE,{"disambiguationData":[TD([[makeQuery(id+"F1.imprint","IMPRINT",EDGE,{"disambiguationData":[TD([[subQ2,-1.0]])],"derivedFrom":subQ1}),1.0]])]});}
            var Q2;
            {var subQ0=sQuery(id+"F1.wireOp",EDGE,"E64");var subQ1=sQuery(id+"F1.wireOp",EDGE,"E58.8.0");var subQ2=makeQuery(id+"F1.imprint","INTERSECT",VERTEX,{"derivedFrom":[subQ1,subQ0]});Q2=makeQuery(id+"F1.imprint","IMPRINT",FACE,{"disambiguationData":[TD([[makeQuery(id+"F1.imprint","IMPRINT",EDGE,{"disambiguationData":[TD([[subQ2,-1.0]])],"derivedFrom":subQ1}),-1.0]])]});}
            var Q3;
            {var subQ0=sQuery(id+"F1.wireOp",EDGE,"E64");var subQ1=sQuery(id+"F1.wireOp",EDGE,"E58.10.0");var subQ2=makeQuery(id+"F1.imprint","INTERSECT",VERTEX,{"derivedFrom":[subQ1,subQ0]});Q3=makeQuery(id+"F1.imprint","IMPRINT",FACE,{"disambiguationData":[TD([[makeQuery(id+"F1.imprint","IMPRINT",EDGE,{"disambiguationData":[TD([[subQ2,-1.0]])],"derivedFrom":subQ1}),-1.0]])]});}
            var Q4;
            {var subQ0=sQuery(id+"F1.wireOp",EDGE,"E64");var subQ1=sQuery(id+"F1.wireOp",EDGE,"E58.8.1");var subQ2=makeQuery(id+"F1.imprint","INTERSECT",VERTEX,{"derivedFrom":[subQ1,subQ0]});Q4=makeQuery(id+"F1.imprint","IMPRINT",FACE,{"disambiguationData":[TD([[makeQuery(id+"F1.imprint","IMPRINT",EDGE,{"disambiguationData":[TD([[subQ2,-1.0]])],"derivedFrom":subQ1}),1.0]])]});}
            var Q5;
            {var subQ0=sQuery(id+"F1.wireOp",EDGE,"E64");var subQ1=sQuery(id+"F1.wireOp",EDGE,"E58.5.1");var subQ2=makeQuery(id+"F1.imprint","INTERSECT",VERTEX,{"derivedFrom":[subQ1,subQ0]});Q5=makeQuery(id+"F1.imprint","IMPRINT",FACE,{"disambiguationData":[TD([[makeQuery(id+"F1.imprint","IMPRINT",EDGE,{"disambiguationData":[TD([[subQ2,-1.0]])],"derivedFrom":subQ1}),1.0]])]});}
            var Q6;
            {var subQ0=sQuery(id+"F1.wireOp",EDGE,"E64");var subQ1=sQuery(id+"F1.wireOp",EDGE,"E58.4.0");var subQ2=makeQuery(id+"F1.imprint","INTERSECT",VERTEX,{"derivedFrom":[subQ1,subQ0]});Q6=makeQuery(id+"F1.imprint","IMPRINT",FACE,{"disambiguationData":[TD([[makeQuery(id+"F1.imprint","IMPRINT",EDGE,{"disambiguationData":[TD([[subQ2,-1.0]])],"derivedFrom":subQ1}),-1.0]])]});}
            var Q7;
            {var subQ0=sQuery(id+"F1.wireOp",EDGE,"E64");var subQ1=sQuery(id+"F1.wireOp",EDGE,"E58.5.0");var subQ2=makeQuery(id+"F1.imprint","INTERSECT",VERTEX,{"derivedFrom":[subQ1,subQ0]});Q7=makeQuery(id+"F1.imprint","IMPRINT",FACE,{"disambiguationData":[TD([[makeQuery(id+"F1.imprint","IMPRINT",EDGE,{"disambiguationData":[TD([[subQ2,-1.0]])],"derivedFrom":subQ1}),-1.0]])]});}
            var Q8;
            {var subQ0=sQuery(id+"F1.wireOp",EDGE,"E64");var subQ1=sQuery(id+"F1.wireOp",EDGE,"E58.12.0");var subQ2=makeQuery(id+"F1.imprint","INTERSECT",VERTEX,{"derivedFrom":[subQ1,subQ0]});Q8=makeQuery(id+"F1.imprint","IMPRINT",FACE,{"disambiguationData":[TD([[makeQuery(id+"F1.imprint","IMPRINT",EDGE,{"disambiguationData":[TD([[subQ2,-1.0]])],"derivedFrom":subQ1}),-1.0]])]});}
            var Q9;
            {var subQ0=sQuery(id+"F1.wireOp",EDGE,"E64");var subQ1=sQuery(id+"F1.wireOp",EDGE,"E58.9.1");var subQ2=makeQuery(id+"F1.imprint","INTERSECT",VERTEX,{"derivedFrom":[subQ1,subQ0]});Q9=makeQuery(id+"F1.imprint","IMPRINT",FACE,{"disambiguationData":[TD([[makeQuery(id+"F1.imprint","IMPRINT",EDGE,{"disambiguationData":[TD([[subQ2,-1.0]])],"derivedFrom":subQ1}),1.0]])]});}
            var Q10;
            {var subQ0=sQuery(id+"F1.wireOp",EDGE,"E64");var subQ1=sQuery(id+"F1.wireOp",EDGE,"E58.9.0");var subQ2=makeQuery(id+"F1.imprint","INTERSECT",VERTEX,{"derivedFrom":[subQ1,subQ0]});Q10=makeQuery(id+"F1.imprint","IMPRINT",FACE,{"disambiguationData":[TD([[makeQuery(id+"F1.imprint","IMPRINT",EDGE,{"disambiguationData":[TD([[subQ2,-1.0]])],"derivedFrom":subQ1}),-1.0]])]});}
            var Q11;
            {var subQ0=sQuery(id+"F1.wireOp",EDGE,"E64");var subQ1=sQuery(id+"F1.wireOp",EDGE,"E58.11.0");var subQ2=makeQuery(id+"F1.imprint","INTERSECT",VERTEX,{"derivedFrom":[subQ1,subQ0]});Q11=makeQuery(id+"F1.imprint","IMPRINT",FACE,{"disambiguationData":[TD([[makeQuery(id+"F1.imprint","IMPRINT",EDGE,{"disambiguationData":[TD([[subQ2,-1.0]])],"derivedFrom":subQ1}),-1.0]])]});}
            var Q12;
            {var subQ0=sQuery(id+"F1.wireOp",EDGE,"E64");var subQ1=sQuery(id+"F1.wireOp",EDGE,"E58.6.1");var subQ2=makeQuery(id+"F1.imprint","INTERSECT",VERTEX,{"derivedFrom":[subQ1,subQ0]});Q12=makeQuery(id+"F1.imprint","IMPRINT",FACE,{"disambiguationData":[TD([[makeQuery(id+"F1.imprint","IMPRINT",EDGE,{"disambiguationData":[TD([[subQ2,-1.0]])],"derivedFrom":subQ1}),1.0]])]});}
            var Q13;
            {var subQ0=sQuery(id+"F1.wireOp",EDGE,"E64");var subQ1=sQuery(id+"F1.wireOp",EDGE,"E58.4.0");var subQ2=makeQuery(id+"F1.imprint","INTERSECT",VERTEX,{"derivedFrom":[subQ1,subQ0]});Q13=makeQuery(id+"F1.imprint","IMPRINT",FACE,{"disambiguationData":[TD([[makeQuery(id+"F1.imprint","IMPRINT",EDGE,{"disambiguationData":[TD([[subQ2,-1.0]])],"derivedFrom":subQ1}),1.0]])]});}
            var Q14;
            {var subQ0=sQuery(id+"F1.wireOp",EDGE,"E64");var subQ1=sQuery(id+"F1.wireOp",EDGE,"E58.7.0");var subQ2=makeQuery(id+"F1.imprint","INTERSECT",VERTEX,{"derivedFrom":[subQ1,subQ0]});Q14=makeQuery(id+"F1.imprint","IMPRINT",FACE,{"disambiguationData":[TD([[makeQuery(id+"F1.imprint","IMPRINT",EDGE,{"disambiguationData":[TD([[subQ2,-1.0]])],"derivedFrom":subQ1}),-1.0]])]});}
            var Q15;
            {var subQ0=sQuery(id+"F1.wireOp",EDGE,"E64");var subQ1=sQuery(id+"F1.wireOp",EDGE,"E58.4.1");var subQ2=makeQuery(id+"F1.imprint","INTERSECT",VERTEX,{"derivedFrom":[subQ1,subQ0]});Q15=makeQuery(id+"F1.imprint","IMPRINT",FACE,{"disambiguationData":[TD([[makeQuery(id+"F1.imprint","IMPRINT",EDGE,{"disambiguationData":[TD([[subQ2,-1.0]])],"derivedFrom":subQ1}),1.0]])]});}
            var Q16;
            {var subQ0=sQuery(id+"F1.wireOp",EDGE,"E64");var subQ1=sQuery(id+"F1.wireOp",EDGE,"E58.6.0");var subQ2=makeQuery(id+"F1.imprint","INTERSECT",VERTEX,{"derivedFrom":[subQ1,subQ0]});Q16=makeQuery(id+"F1.imprint","IMPRINT",FACE,{"disambiguationData":[TD([[makeQuery(id+"F1.imprint","IMPRINT",EDGE,{"disambiguationData":[TD([[subQ2,-1.0]])],"derivedFrom":subQ1}),-1.0]])]});}
            var Q17;
            {var subQ0=sQuery(id+"F1.wireOp",EDGE,"E64");var subQ1=sQuery(id+"F1.wireOp",EDGE,"E58.10.0");var subQ2=makeQuery(id+"F1.imprint","INTERSECT",VERTEX,{"derivedFrom":[subQ1,subQ0]});Q17=makeQuery(id+"F1.imprint","IMPRINT",FACE,{"disambiguationData":[TD([[makeQuery(id+"F1.imprint","IMPRINT",EDGE,{"disambiguationData":[TD([[subQ2,-1.0]])],"derivedFrom":subQ1}),1.0]])]});}
            var Q18;
            {var subQ0=sQuery(id+"F1.wireOp",EDGE,"E64");var subQ1=sQuery(id+"F1.wireOp",EDGE,"E58.10.1");var subQ2=makeQuery(id+"F1.imprint","INTERSECT",VERTEX,{"derivedFrom":[subQ1,subQ0]});Q18=makeQuery(id+"F1.imprint","IMPRINT",FACE,{"disambiguationData":[TD([[makeQuery(id+"F1.imprint","IMPRINT",EDGE,{"disambiguationData":[TD([[subQ2,-1.0]])],"derivedFrom":subQ1}),1.0]])]});}
            var Q19;
            {var subQ0=sQuery(id+"F1.wireOp",EDGE,"E64");var subQ1=sQuery(id+"F1.wireOp",EDGE,"E58.4.2");var subQ2=makeQuery(id+"F1.imprint","INTERSECT",VERTEX,{"derivedFrom":[subQ1,subQ0]});Q19=makeQuery(id+"F1.imprint","IMPRINT",FACE,{"disambiguationData":[TD([[makeQuery(id+"F1.imprint","IMPRINT",EDGE,{"disambiguationData":[TD([[subQ2,-1.0]])],"derivedFrom":subQ1}),-1.0]])]});}
            var Q20;
            {var subQ0=sQuery(id+"F1.wireOp",EDGE,"E64");var subQ1=sQuery(id+"F1.wireOp",EDGE,"E58.5.0");var subQ2=makeQuery(id+"F1.imprint","INTERSECT",VERTEX,{"derivedFrom":[subQ1,subQ0]});Q20=makeQuery(id+"F1.imprint","IMPRINT",FACE,{"disambiguationData":[TD([[makeQuery(id+"F1.imprint","IMPRINT",EDGE,{"disambiguationData":[TD([[subQ2,-1.0]])],"derivedFrom":subQ1}),1.0]])]});}
            var Q21;
            {var subQ0=sQuery(id+"F1.wireOp",EDGE,"E64");var subQ1=sQuery(id+"F1.wireOp",EDGE,"E58.7.0");var subQ2=makeQuery(id+"F1.imprint","INTERSECT",VERTEX,{"derivedFrom":[subQ1,subQ0]});Q21=makeQuery(id+"F1.imprint","IMPRINT",FACE,{"disambiguationData":[TD([[makeQuery(id+"F1.imprint","IMPRINT",EDGE,{"disambiguationData":[TD([[subQ2,-1.0]])],"derivedFrom":subQ1}),1.0]])]});}
            var Q22;
            {var subQ0=sQuery(id+"F1.wireOp",EDGE,"E64");var subQ1=sQuery(id+"F1.wireOp",EDGE,"E58.9.0");var subQ2=makeQuery(id+"F1.imprint","INTERSECT",VERTEX,{"derivedFrom":[subQ1,subQ0]});Q22=makeQuery(id+"F1.imprint","IMPRINT",FACE,{"disambiguationData":[TD([[makeQuery(id+"F1.imprint","IMPRINT",EDGE,{"disambiguationData":[TD([[subQ2,-1.0]])],"derivedFrom":subQ1}),1.0]])]});}
            var Q23;
            {var subQ0=sQuery(id+"F1.wireOp",EDGE,"E64");var subQ1=sQuery(id+"F1.wireOp",EDGE,"E58.12.0");var subQ2=makeQuery(id+"F1.imprint","INTERSECT",VERTEX,{"derivedFrom":[subQ1,subQ0]});Q23=makeQuery(id+"F1.imprint","IMPRINT",FACE,{"disambiguationData":[TD([[makeQuery(id+"F1.imprint","IMPRINT",EDGE,{"disambiguationData":[TD([[subQ2,-1.0]])],"derivedFrom":subQ1}),1.0]])]});}
            var Q24;
            {var subQ0=sQuery(id+"F1.wireOp",EDGE,"E64");var subQ1=sQuery(id+"F1.wireOp",EDGE,"E58.8.0");var subQ2=makeQuery(id+"F1.imprint","INTERSECT",VERTEX,{"derivedFrom":[subQ1,subQ0]});Q24=makeQuery(id+"F1.imprint","IMPRINT",FACE,{"disambiguationData":[TD([[makeQuery(id+"F1.imprint","IMPRINT",EDGE,{"disambiguationData":[TD([[subQ2,-1.0]])],"derivedFrom":subQ1}),1.0]])]});}
            var Q25;
            {var subQ0=sQuery(id+"F1.wireOp",EDGE,"E64");var subQ1=sQuery(id+"F1.wireOp",EDGE,"E58.7.1");var subQ2=makeQuery(id+"F1.imprint","INTERSECT",VERTEX,{"derivedFrom":[subQ1,subQ0]});Q25=makeQuery(id+"F1.imprint","IMPRINT",FACE,{"disambiguationData":[TD([[makeQuery(id+"F1.imprint","IMPRINT",EDGE,{"disambiguationData":[TD([[subQ2,-1.0]])],"derivedFrom":subQ1}),1.0]])]});}
            var Q26;
            {var subQ0=sQuery(id+"F1.wireOp",EDGE,"E64");var subQ1=sQuery(id+"F1.wireOp",EDGE,"E58.11.0");var subQ2=makeQuery(id+"F1.imprint","INTERSECT",VERTEX,{"derivedFrom":[subQ1,subQ0]});Q26=makeQuery(id+"F1.imprint","IMPRINT",FACE,{"disambiguationData":[TD([[makeQuery(id+"F1.imprint","IMPRINT",EDGE,{"disambiguationData":[TD([[subQ2,-1.0]])],"derivedFrom":subQ1}),1.0]])]});}
            extrude(context, id + "F13", {"entities" : qUnion([Q0, Q1, Q2, Q3, Q4, Q5, Q6, Q7, Q8, Q9, Q10, Q11, Q12, Q13, Q14, Q15, Q16, Q17, Q18, Q19, Q20, Q21, Q22, Q23, Q24, Q25, Q26]), "operationType" : NewBodyOperationType.ADD, "oppositeDirection" : true, "depth" : 1092.2 * mm, "offsetDistance" : 25.4 * mm, "hasSecondDirection" : true, "secondDirectionOppositeDirection" : true, "secondDirectionDepth" : 1016 * mm});
        }
        {
            var Q0;
            {var subQ0=sQuery(id+"F1.wireOp",EDGE,"E58.9.0");var subQ1=sQuery(id+"F1.wireOp",EDGE,"E57");var subQ2=makeQuery(id+"F1.imprint","INTERSECT",VERTEX,{"derivedFrom":[subQ1,subQ0]});Q0=makeQuery(id+"F1.imprint","IMPRINT",FACE,{"disambiguationData":[TD([[makeQuery(id+"F1.imprint","IMPRINT",EDGE,{"disambiguationData":[TD([[subQ2,1.0]])],"derivedFrom":subQ1}),1.0]])]});}
            var Q1;
            {var subQ0=sQuery(id+"F1.wireOp",EDGE,"E58.10.0");var subQ1=sQuery(id+"F1.wireOp",EDGE,"E57");var subQ2=makeQuery(id+"F1.imprint","INTERSECT",VERTEX,{"derivedFrom":[subQ1,subQ0]});Q1=makeQuery(id+"F1.imprint","IMPRINT",FACE,{"disambiguationData":[TD([[makeQuery(id+"F1.imprint","IMPRINT",EDGE,{"disambiguationData":[TD([[subQ2,-1.0]])],"derivedFrom":subQ1}),1.0]])]});}
            var Q2;
            {var subQ0=sQuery(id+"F1.wireOp",EDGE,"E58.6.0");var subQ1=sQuery(id+"F1.wireOp",EDGE,"E57");var subQ2=makeQuery(id+"F1.imprint","INTERSECT",VERTEX,{"derivedFrom":[subQ1,subQ0]});Q2=makeQuery(id+"F1.imprint","IMPRINT",FACE,{"disambiguationData":[TD([[makeQuery(id+"F1.imprint","IMPRINT",EDGE,{"disambiguationData":[TD([[subQ2,-1.0]])],"derivedFrom":subQ1}),1.0]])]});}
            var Q3;
            {var subQ0=sQuery(id+"F1.wireOp",EDGE,"E58.4.0");var subQ1=sQuery(id+"F1.wireOp",EDGE,"E55");var subQ2=makeQuery(id+"F1.imprint","INTERSECT",VERTEX,{"derivedFrom":[subQ1,subQ0]});Q3=makeQuery(id+"F1.imprint","IMPRINT",FACE,{"disambiguationData":[TD([[makeQuery(id+"F1.imprint","IMPRINT",EDGE,{"disambiguationData":[TD([[subQ2,-1.0]])],"derivedFrom":subQ1}),-1.0]])]});}
            var Q4;
            {var subQ0=sQuery(id+"F1.wireOp",EDGE,"E58.4.1");var subQ1=sQuery(id+"F1.wireOp",EDGE,"E57");var subQ2=makeQuery(id+"F1.imprint","INTERSECT",VERTEX,{"derivedFrom":[subQ1,subQ0]});Q4=makeQuery(id+"F1.imprint","IMPRINT",FACE,{"disambiguationData":[TD([[makeQuery(id+"F1.imprint","IMPRINT",EDGE,{"disambiguationData":[TD([[subQ2,1.0]])],"derivedFrom":subQ1}),1.0]])]});}
            var Q5;
            {var subQ0=sQuery(id+"F1.wireOp",EDGE,"E58.6.1");var subQ1=sQuery(id+"F1.wireOp",EDGE,"E57");var subQ2=makeQuery(id+"F1.imprint","INTERSECT",VERTEX,{"derivedFrom":[subQ1,subQ0]});Q5=makeQuery(id+"F1.imprint","IMPRINT",FACE,{"disambiguationData":[TD([[makeQuery(id+"F1.imprint","IMPRINT",EDGE,{"disambiguationData":[TD([[subQ2,-1.0]])],"derivedFrom":subQ1}),1.0]])]});}
            var Q6;
            {var subQ0=sQuery(id+"F1.wireOp",EDGE,"E58.11.0");var subQ1=sQuery(id+"F1.wireOp",EDGE,"E57");var subQ2=makeQuery(id+"F1.imprint","INTERSECT",VERTEX,{"derivedFrom":[subQ1,subQ0]});Q6=makeQuery(id+"F1.imprint","IMPRINT",FACE,{"disambiguationData":[TD([[makeQuery(id+"F1.imprint","IMPRINT",EDGE,{"disambiguationData":[TD([[subQ2,1.0]])],"derivedFrom":subQ1}),1.0]])]});}
            var Q7;
            {var subQ0=sQuery(id+"F1.wireOp",EDGE,"E58.12.1");var subQ1=sQuery(id+"F1.wireOp",EDGE,"E57");var subQ2=makeQuery(id+"F1.imprint","INTERSECT",VERTEX,{"derivedFrom":[subQ1,subQ0]});Q7=makeQuery(id+"F1.imprint","IMPRINT",FACE,{"disambiguationData":[TD([[makeQuery(id+"F1.imprint","IMPRINT",EDGE,{"disambiguationData":[TD([[subQ2,1.0]])],"derivedFrom":subQ1}),1.0]])]});}
            var Q8;
            {var subQ0=sQuery(id+"F1.wireOp",EDGE,"E58.12.2");var subQ1=sQuery(id+"F1.wireOp",EDGE,"E57");var subQ2=makeQuery(id+"F1.imprint","INTERSECT",VERTEX,{"derivedFrom":[subQ1,subQ0]});Q8=makeQuery(id+"F1.imprint","IMPRINT",FACE,{"disambiguationData":[TD([[makeQuery(id+"F1.imprint","IMPRINT",EDGE,{"disambiguationData":[TD([[subQ2,-1.0]])],"derivedFrom":subQ1}),1.0]])]});}
            var Q9;
            Q9=makeQuery(id+"F1.imprint","IMPRINT",FACE,{"disambiguationData":[TD([[makeQuery(id+"F1.imprint","IMPRINT",EDGE,{"derivedFrom":sQuery(id+"F1.wireOp",EDGE,"E66")}),1.0]])]});
            var Q10;
            {var subQ17=sQuery(id+"F1.wireOp",EDGE,"E58.4.0");var subQ19=sQuery(id+"F1.wireOp",EDGE,"E55");var subQ20=makeQuery(id+"F1.imprint","INTERSECT",VERTEX,{"derivedFrom":[subQ19,subQ17]});Q10=makeQuery(id+"F1.imprint","IMPRINT",FACE,{"disambiguationData":[TD([[makeQuery(id+"F1.imprint","IMPRINT",EDGE,{"disambiguationData":[TD([[subQ20,-1.0]])],"derivedFrom":subQ19}),1.0]])]});}
            var Q11;
            {var subQ0=sQuery(id+"F1.wireOp",EDGE,"E58.5.0");var subQ1=sQuery(id+"F1.wireOp",EDGE,"E57");var subQ2=makeQuery(id+"F1.imprint","INTERSECT",VERTEX,{"derivedFrom":[subQ1,subQ0]});Q11=makeQuery(id+"F1.imprint","IMPRINT",FACE,{"disambiguationData":[TD([[makeQuery(id+"F1.imprint","IMPRINT",EDGE,{"disambiguationData":[TD([[subQ2,-1.0]])],"derivedFrom":subQ1}),1.0]])]});}
            var Q12;
            {var subQ0=sQuery(id+"F1.wireOp",EDGE,"E58.7.0");var subQ1=sQuery(id+"F1.wireOp",EDGE,"E57");var subQ2=makeQuery(id+"F1.imprint","INTERSECT",VERTEX,{"derivedFrom":[subQ1,subQ0]});Q12=makeQuery(id+"F1.imprint","IMPRINT",FACE,{"disambiguationData":[TD([[makeQuery(id+"F1.imprint","IMPRINT",EDGE,{"disambiguationData":[TD([[subQ2,1.0]])],"derivedFrom":subQ1}),1.0]])]});}
            var Q13;
            {var subQ0=sQuery(id+"F1.wireOp",EDGE,"E58.8.1");var subQ1=sQuery(id+"F1.wireOp",EDGE,"E57");var subQ2=makeQuery(id+"F1.imprint","INTERSECT",VERTEX,{"derivedFrom":[subQ1,subQ0]});Q13=makeQuery(id+"F1.imprint","IMPRINT",FACE,{"disambiguationData":[TD([[makeQuery(id+"F1.imprint","IMPRINT",EDGE,{"disambiguationData":[TD([[subQ2,-1.0]])],"derivedFrom":subQ1}),1.0]])]});}
            var Q14;
            {var subQ0=sQuery(id+"F1.wireOp",EDGE,"E58.8.0");var subQ1=sQuery(id+"F1.wireOp",EDGE,"E57");var subQ2=makeQuery(id+"F1.imprint","INTERSECT",VERTEX,{"derivedFrom":[subQ1,subQ0]});Q14=makeQuery(id+"F1.imprint","IMPRINT",FACE,{"disambiguationData":[TD([[makeQuery(id+"F1.imprint","IMPRINT",EDGE,{"disambiguationData":[TD([[subQ2,1.0]])],"derivedFrom":subQ1}),1.0]])]});}
            var Q15;
            {var subQ0=sQuery(id+"F1.wireOp",EDGE,"E58.4.0");var subQ1=sQuery(id+"F1.wireOp",EDGE,"E55");var subQ2=makeQuery(id+"F1.imprint","INTERSECT",VERTEX,{"derivedFrom":[subQ1,subQ0]});Q15=makeQuery(id+"F1.imprint","IMPRINT",FACE,{"disambiguationData":[TD([[makeQuery(id+"F1.imprint","IMPRINT",EDGE,{"disambiguationData":[TD([[subQ2,1.0]])],"derivedFrom":subQ1}),-1.0]])]});}
            var Q16;
            {var subQ0=sQuery(id+"F1.wireOp",EDGE,"E58.10.1");var subQ1=sQuery(id+"F1.wireOp",EDGE,"E57");var subQ2=makeQuery(id+"F1.imprint","INTERSECT",VERTEX,{"derivedFrom":[subQ1,subQ0]});Q16=makeQuery(id+"F1.imprint","IMPRINT",FACE,{"disambiguationData":[TD([[makeQuery(id+"F1.imprint","IMPRINT",EDGE,{"disambiguationData":[TD([[subQ2,-1.0]])],"derivedFrom":subQ1}),1.0]])]});}
            var Q17;
            {var subQ0=sQuery(id+"F1.wireOp",EDGE,"E58.7.1");var subQ1=sQuery(id+"F1.wireOp",EDGE,"E57");var subQ2=makeQuery(id+"F1.imprint","INTERSECT",VERTEX,{"derivedFrom":[subQ1,subQ0]});Q17=makeQuery(id+"F1.imprint","IMPRINT",FACE,{"disambiguationData":[TD([[makeQuery(id+"F1.imprint","IMPRINT",EDGE,{"disambiguationData":[TD([[subQ2,-1.0]])],"derivedFrom":subQ1}),1.0]])]});}
            var Q18;
            {var subQ0=sQuery(id+"F1.wireOp",EDGE,"E58.8.0");var subQ1=sQuery(id+"F1.wireOp",EDGE,"E57");var subQ2=makeQuery(id+"F1.imprint","INTERSECT",VERTEX,{"derivedFrom":[subQ1,subQ0]});Q18=makeQuery(id+"F1.imprint","IMPRINT",FACE,{"disambiguationData":[TD([[makeQuery(id+"F1.imprint","IMPRINT",EDGE,{"disambiguationData":[TD([[subQ2,-1.0]])],"derivedFrom":subQ1}),1.0]])]});}
            var Q19;
            {var subQ0=sQuery(id+"F1.wireOp",EDGE,"E58.11.0");var subQ1=sQuery(id+"F1.wireOp",EDGE,"E57");var subQ2=makeQuery(id+"F1.imprint","INTERSECT",VERTEX,{"derivedFrom":[subQ1,subQ0]});Q19=makeQuery(id+"F1.imprint","IMPRINT",FACE,{"disambiguationData":[TD([[makeQuery(id+"F1.imprint","IMPRINT",EDGE,{"disambiguationData":[TD([[subQ2,-1.0]])],"derivedFrom":subQ1}),1.0]])]});}
            var Q20;
            {var subQ0=sQuery(id+"F1.wireOp",EDGE,"E58.4.2");var subQ1=sQuery(id+"F1.wireOp",EDGE,"E57");var subQ2=makeQuery(id+"F1.imprint","INTERSECT",VERTEX,{"derivedFrom":[subQ1,subQ0]});Q20=makeQuery(id+"F1.imprint","IMPRINT",FACE,{"disambiguationData":[TD([[makeQuery(id+"F1.imprint","IMPRINT",EDGE,{"disambiguationData":[TD([[subQ2,-1.0]])],"derivedFrom":subQ1}),1.0]])]});}
            var Q21;
            {var subQ0=sQuery(id+"F1.wireOp",EDGE,"E58.5.0");var subQ1=sQuery(id+"F1.wireOp",EDGE,"E57");var subQ2=makeQuery(id+"F1.imprint","INTERSECT",VERTEX,{"derivedFrom":[subQ1,subQ0]});Q21=makeQuery(id+"F1.imprint","IMPRINT",FACE,{"disambiguationData":[TD([[makeQuery(id+"F1.imprint","IMPRINT",EDGE,{"disambiguationData":[TD([[subQ2,1.0]])],"derivedFrom":subQ1}),1.0]])]});}
            var Q22;
            {var subQ0=sQuery(id+"F1.wireOp",EDGE,"E58.7.0");var subQ1=sQuery(id+"F1.wireOp",EDGE,"E57");var subQ2=makeQuery(id+"F1.imprint","INTERSECT",VERTEX,{"derivedFrom":[subQ1,subQ0]});Q22=makeQuery(id+"F1.imprint","IMPRINT",FACE,{"disambiguationData":[TD([[makeQuery(id+"F1.imprint","IMPRINT",EDGE,{"disambiguationData":[TD([[subQ2,-1.0]])],"derivedFrom":subQ1}),1.0]])]});}
            var Q23;
            {var subQ0=sQuery(id+"F1.wireOp",EDGE,"E58.6.0");var subQ1=sQuery(id+"F1.wireOp",EDGE,"E57");var subQ2=makeQuery(id+"F1.imprint","INTERSECT",VERTEX,{"derivedFrom":[subQ1,subQ0]});Q23=makeQuery(id+"F1.imprint","IMPRINT",FACE,{"disambiguationData":[TD([[makeQuery(id+"F1.imprint","IMPRINT",EDGE,{"disambiguationData":[TD([[subQ2,1.0]])],"derivedFrom":subQ1}),1.0]])]});}
            var Q24;
            {var subQ0=sQuery(id+"F1.wireOp",EDGE,"E58.10.0");var subQ1=sQuery(id+"F1.wireOp",EDGE,"E57");var subQ2=makeQuery(id+"F1.imprint","INTERSECT",VERTEX,{"derivedFrom":[subQ1,subQ0]});Q24=makeQuery(id+"F1.imprint","IMPRINT",FACE,{"disambiguationData":[TD([[makeQuery(id+"F1.imprint","IMPRINT",EDGE,{"disambiguationData":[TD([[subQ2,1.0]])],"derivedFrom":subQ1}),1.0]])]});}
            var Q25;
            {var subQ0=sQuery(id+"F1.wireOp",EDGE,"E58.5.1");var subQ1=sQuery(id+"F1.wireOp",EDGE,"E57");var subQ2=makeQuery(id+"F1.imprint","INTERSECT",VERTEX,{"derivedFrom":[subQ1,subQ0]});Q25=makeQuery(id+"F1.imprint","IMPRINT",FACE,{"disambiguationData":[TD([[makeQuery(id+"F1.imprint","IMPRINT",EDGE,{"disambiguationData":[TD([[subQ2,-1.0]])],"derivedFrom":subQ1}),1.0]])]});}
            var Q26;
            {var subQ0=sQuery(id+"F1.wireOp",EDGE,"E58.9.0");var subQ1=sQuery(id+"F1.wireOp",EDGE,"E57");var subQ2=makeQuery(id+"F1.imprint","INTERSECT",VERTEX,{"derivedFrom":[subQ1,subQ0]});Q26=makeQuery(id+"F1.imprint","IMPRINT",FACE,{"disambiguationData":[TD([[makeQuery(id+"F1.imprint","IMPRINT",EDGE,{"disambiguationData":[TD([[subQ2,-1.0]])],"derivedFrom":subQ1}),1.0]])]});}
            var Q27;
            {var subQ0=sQuery(id+"F1.wireOp",EDGE,"E58.9.1");var subQ1=sQuery(id+"F1.wireOp",EDGE,"E57");var subQ2=makeQuery(id+"F1.imprint","INTERSECT",VERTEX,{"derivedFrom":[subQ1,subQ0]});Q27=makeQuery(id+"F1.imprint","IMPRINT",FACE,{"disambiguationData":[TD([[makeQuery(id+"F1.imprint","IMPRINT",EDGE,{"disambiguationData":[TD([[subQ2,-1.0]])],"derivedFrom":subQ1}),1.0]])]});}
            var Q28;
            {var subQ0=sQuery(id+"F1.wireOp",EDGE,"E58.4.1");var subQ1=sQuery(id+"F1.wireOp",EDGE,"E57");var subQ2=makeQuery(id+"F1.imprint","INTERSECT",VERTEX,{"derivedFrom":[subQ1,subQ0]});Q28=makeQuery(id+"F1.imprint","IMPRINT",FACE,{"disambiguationData":[TD([[makeQuery(id+"F1.imprint","IMPRINT",EDGE,{"disambiguationData":[TD([[subQ2,-1.0]])],"derivedFrom":subQ1}),1.0]])]});}
            var Q29;
            {var subQ5=sQuery(id+"F1.wireOp",EDGE,"E58.4.0");var subQ7=sQuery(id+"F1.wireOp",EDGE,"E55");var subQ8=makeQuery(id+"F1.imprint","INTERSECT",VERTEX,{"derivedFrom":[subQ7,subQ5]});Q29=makeQuery(id+"F1.imprint","IMPRINT",FACE,{"disambiguationData":[TD([[makeQuery(id+"F1.imprint","IMPRINT",EDGE,{"disambiguationData":[TD([[subQ8,1.0]])],"derivedFrom":subQ7}),1.0]])]});}
            var Q30;
            {var subQ0=sQuery(id+"F1.wireOp",EDGE,"E58.11.1");var subQ1=sQuery(id+"F1.wireOp",EDGE,"E57");var subQ2=makeQuery(id+"F1.imprint","INTERSECT",VERTEX,{"derivedFrom":[subQ1,subQ0]});Q30=makeQuery(id+"F1.imprint","IMPRINT",FACE,{"disambiguationData":[TD([[makeQuery(id+"F1.imprint","IMPRINT",EDGE,{"disambiguationData":[TD([[subQ2,-1.0]])],"derivedFrom":subQ1}),1.0]])]});}
            var Q31;
            {var subQ0=sQuery(id+"F1.wireOp",EDGE,"E58.4.2");var subQ1=sQuery(id+"F1.wireOp",EDGE,"E57");var subQ2=makeQuery(id+"F1.imprint","INTERSECT",VERTEX,{"derivedFrom":[subQ1,subQ0]});Q31=makeQuery(id+"F1.imprint","IMPRINT",FACE,{"disambiguationData":[TD([[makeQuery(id+"F1.imprint","IMPRINT",EDGE,{"disambiguationData":[TD([[subQ2,1.0]])],"derivedFrom":subQ1}),1.0]])]});}
            extrude(context, id + "F14", {"entities" : qUnion([Q0, Q1, Q2, Q3, Q4, Q5, Q6, Q7, Q8, Q9, Q10, Q11, Q12, Q13, Q14, Q15, Q16, Q17, Q18, Q19, Q20, Q21, Q22, Q23, Q24, Q25, Q26, Q27, Q28, Q29, Q30, Q31]), "operationType" : NewBodyOperationType.ADD, "oppositeDirection" : true, "depth" : 1025.52 * mm, "offsetDistance" : 25.4 * mm, "hasSecondDirection" : true, "secondDirectionOppositeDirection" : true, "secondDirectionDepth" : 1022.35 * mm});
        }
        {
            var Q0;
            Q0=qCreatedBy(makeId("Right.planeOp"),FACE);
            var sketch = newSketch(context, id + "F15", { "sketchPlane" : qUnion([Q0])});
            skEllipticalArc(sketch, "E106", {});
            skLineSegment(sketch, "E107", {"start": v(0, -65.5) * mm, "end": v(0, 65.5) * mm});
            skLineSegment(sketch, "E108", {"start": v(-26.28, 2.62) * mm, "end": v(-85.9, 8.56) * mm});
            skFitSpline(sketch, "E109.0", {"points": [v(-83.54, 26.86) * mm, v(-84.45, 24.03) * mm, v(-85.16, 21.15) * mm, v(-85.84, 17.26) * mm, v(-86.18, 12.31) * mm, v(-85.79, 6.26) * mm, v(-84.6, 0.15) * mm, v(-82.62, -6) * mm, v(-80.3, -11.1) * mm, v(-78.07, -15.16) * mm, v(-76.19, -18.17) * mm, v(-74.12, -21.16) * mm, v(-71.85, -24.12) * mm, v(-69.4, -27.02) * mm, v(-66.79, -29.84) * mm, v(-64.02, -32.58) * mm, v(-60.13, -36.12) * mm, v(-54.9, -40.32) * mm, v(-48.11, -44.96) * mm, v(-40.85, -49.17) * mm, v(-34.45, -52.28) * mm, v(-29.14, -54.53) * mm, v(-25.08, -56.08) * mm, v(-21.63, -57.26) * mm, v(-18.84, -58.14) * mm, v(-16.72, -58.76) * mm, v(-14.6, -59.34) * mm, v(-11.76, -60.07) * mm, v(-8.2, -60.88) * mm, v(-3.94, -61.7) * mm, v(1.75, -62.59) * mm, v(8.84, -63.3) * mm, v(17.23, -63.55) * mm, v(25.45, -63.18) * mm, v(32.1, -62.36) * mm, v(37.27, -61.4) * mm, v(41.07, -60.53) * mm, v(44.77, -59.5) * mm, v(48.38, -58.33) * mm, v(51.87, -57.02) * mm, v(55.2, -55.57) * mm, v(58.39, -54) * mm, v(62.43, -51.73) * mm, v(67.08, -48.6) * mm, v(72, -44.42) * mm, v(76.23, -39.85) * mm, v(79.75, -34.91) * mm, v(82.06, -30.52) * mm, v(83.54, -26.86) * mm, v(84.45, -24.03) * mm, v(85.16, -21.15) * mm, v(85.84, -17.26) * mm, v(86.18, -12.31) * mm, v(85.79, -6.26) * mm, v(84.6, -0.15) * mm, v(82.62, 6) * mm, v(80.3, 11.1) * mm, v(78.07, 15.16) * mm, v(76.19, 18.17) * mm, v(74.12, 21.16) * mm, v(71.85, 24.12) * mm, v(69.4, 27.02) * mm, v(66.79, 29.84) * mm, v(64.02, 32.58) * mm, v(60.13, 36.12) * mm, v(54.9, 40.32) * mm, v(48.11, 44.96) * mm, v(40.85, 49.17) * mm, v(34.45, 52.28) * mm, v(29.14, 54.53) * mm, v(25.08, 56.08) * mm, v(21.63, 57.26) * mm, v(18.84, 58.14) * mm, v(16.72, 58.76) * mm, v(14.6, 59.34) * mm, v(11.76, 60.07) * mm, v(8.2, 60.88) * mm, v(3.94, 61.7) * mm, v(-1.75, 62.59) * mm, v(-8.84, 63.3) * mm, v(-17.23, 63.55) * mm, v(-25.45, 63.18) * mm, v(-32.1, 62.36) * mm, v(-37.27, 61.4) * mm, v(-41.07, 60.53) * mm, v(-44.77, 59.5) * mm, v(-48.38, 58.33) * mm, v(-51.87, 57.02) * mm, v(-55.2, 55.57) * mm, v(-58.39, 54) * mm, v(-62.43, 51.73) * mm, v(-67.08, 48.6) * mm, v(-72, 44.42) * mm, v(-76.23, 39.85) * mm, v(-79.75, 34.91) * mm, v(-82.06, 30.52) * mm, v(-83.54, 26.86) * mm, v(-84.45, 24.03) * mm, v(-85.16, 21.15) * mm]});
            skLineSegment(sketch, "E110.0", {"start": v(-3.18, -65.5) * mm, "end": v(-3.18, 65.5) * mm});
            const initialGuessF15  = {"E106": [0, 0, 0.27373290543333084, 0.9618057477905958, 0.06425892814140495, 0.09094469315868683, 0.19844576650476853, 3.340038420094561]};
            skSetInitialGuess(sketch, initialGuessF15);
            skSolve(sketch);
        }
        {
            var Q0;
            {var subQ0=sQuery(id+"F15.wireOp",EDGE,"E110.0");var subQ1=sQuery(id+"F15.wireOp",EDGE,"E106");var subQ2=makeQuery(id+"F15.imprint","INTERSECT",VERTEX,{"derivedFrom":[subQ1,subQ0]});Q0=makeQuery(id+"F15.imprint","IMPRINT",FACE,{"disambiguationData":[TD([[makeQuery(id+"F15.imprint","IMPRINT",EDGE,{"disambiguationData":[TD([[subQ2,1.0]])],"derivedFrom":subQ1}),1.0]])]});}
            extrude(context, id + "F16", {"entities" : qUnion([Q0]), "endBound" : BoundingType.SYMMETRIC, "depth" : 133.35 * mm, "offsetDistance" : 25.4 * mm});
        }
        {
            var Q0;
            {var subQ17=sQuery(id+"F1.wireOp",EDGE,"E58.4.0");var subQ19=sQuery(id+"F1.wireOp",EDGE,"E55");var subQ20=makeQuery(id+"F1.imprint","INTERSECT",VERTEX,{"derivedFrom":[subQ19,subQ17]});Q0=makeQuery(id+"F1.imprint","IMPRINT",FACE,{"disambiguationData":[TD([[makeQuery(id+"F1.imprint","IMPRINT",EDGE,{"disambiguationData":[TD([[subQ20,-1.0]])],"derivedFrom":subQ19}),1.0]])]});}
            var Q1;
            Q1=makeQuery(id+"F1.imprint","IMPRINT",FACE,{"disambiguationData":[TD([[makeQuery(id+"F1.imprint","IMPRINT",EDGE,{"derivedFrom":sQuery(id+"F1.wireOp",EDGE,"E66")}),1.0]])]});
            var Q2;
            {var subQ0=sQuery(id+"F1.wireOp",EDGE,"E58.4.0");var subQ1=sQuery(id+"F1.wireOp",EDGE,"E55");var subQ2=makeQuery(id+"F1.imprint","INTERSECT",VERTEX,{"derivedFrom":[subQ1,subQ0]});Q2=makeQuery(id+"F1.imprint","IMPRINT",FACE,{"disambiguationData":[TD([[makeQuery(id+"F1.imprint","IMPRINT",EDGE,{"disambiguationData":[TD([[subQ2,-1.0]])],"derivedFrom":subQ1}),-1.0]])]});}
            var Q3;
            {var subQ0=sQuery(id+"F1.wireOp",EDGE,"E58.4.0");var subQ1=sQuery(id+"F1.wireOp",EDGE,"E55");var subQ2=makeQuery(id+"F1.imprint","INTERSECT",VERTEX,{"derivedFrom":[subQ1,subQ0]});Q3=makeQuery(id+"F1.imprint","IMPRINT",FACE,{"disambiguationData":[TD([[makeQuery(id+"F1.imprint","IMPRINT",EDGE,{"disambiguationData":[TD([[subQ2,1.0]])],"derivedFrom":subQ1}),-1.0]])]});}
            var Q4;
            {var subQ5=sQuery(id+"F1.wireOp",EDGE,"E58.4.0");var subQ7=sQuery(id+"F1.wireOp",EDGE,"E55");var subQ8=makeQuery(id+"F1.imprint","INTERSECT",VERTEX,{"derivedFrom":[subQ7,subQ5]});Q4=makeQuery(id+"F1.imprint","IMPRINT",FACE,{"disambiguationData":[TD([[makeQuery(id+"F1.imprint","IMPRINT",EDGE,{"disambiguationData":[TD([[subQ8,1.0]])],"derivedFrom":subQ7}),1.0]])]});}
            extrude(context, id + "F17", {"entities" : qUnion([Q0, Q1, Q2, Q3, Q4]), "operationType" : NewBodyOperationType.INTERSECT, "depth" : 101.6 * mm, "offsetDistance" : 25.4 * mm, "hasSecondDirection" : true, "secondDirectionOppositeDirection" : false, "secondDirectionDepth" : 38.1 * mm});
        }
    });
